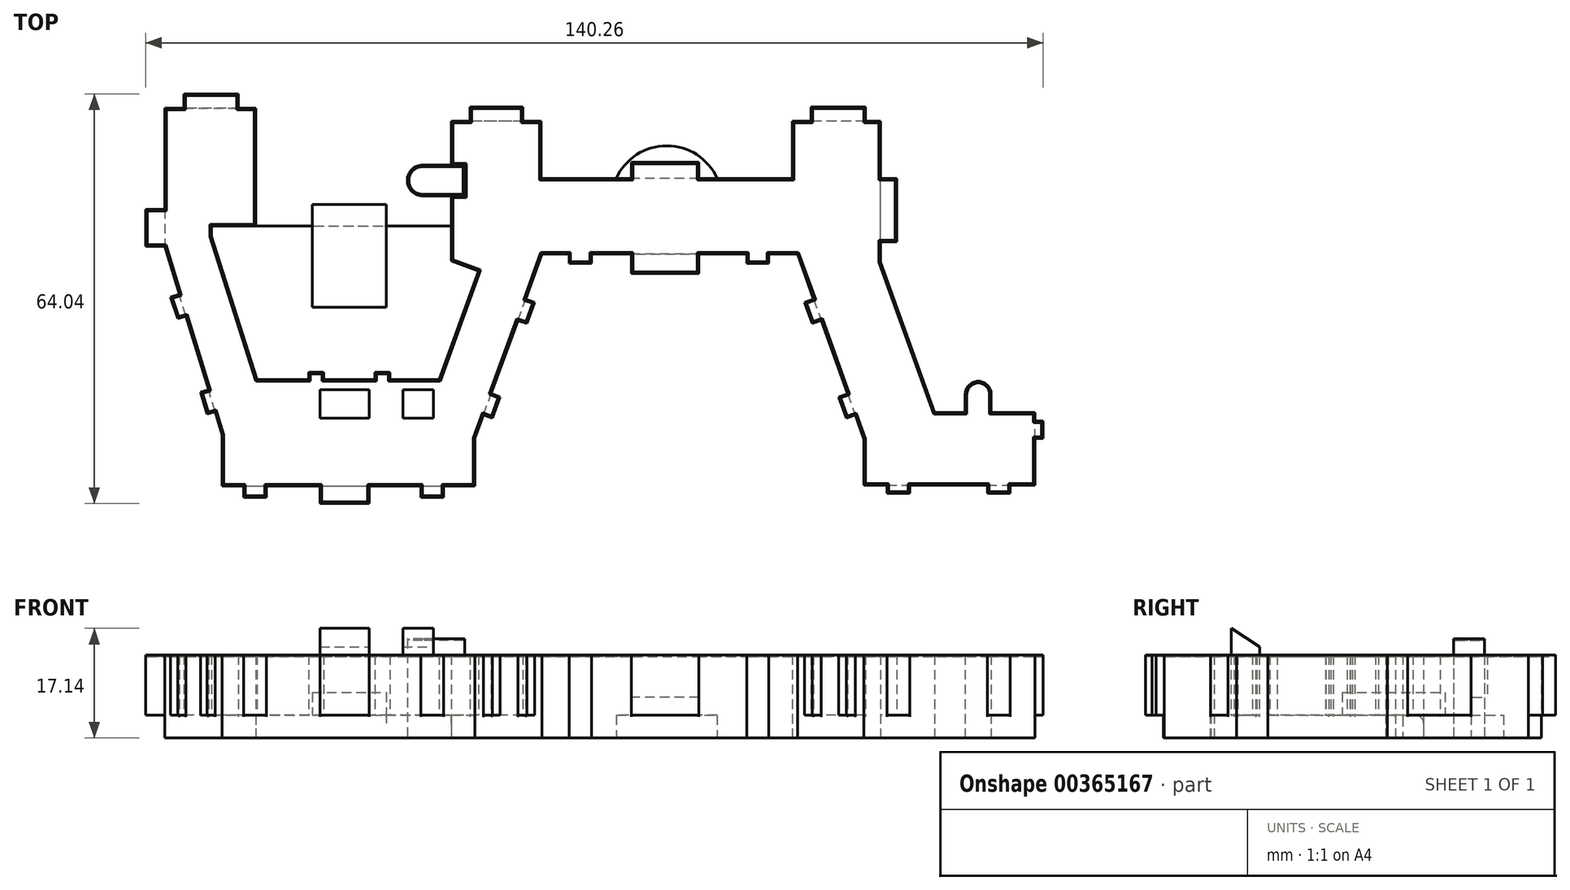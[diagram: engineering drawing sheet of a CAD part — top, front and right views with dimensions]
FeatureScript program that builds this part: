
annotation { "Feature Type Name" : "Feature", "Feature Type Description" : "" }
export const myFeature = defineFeature(function(context is Context, id is Id, definition is map)
    precondition{}
    {
        {
            var Q0;
            Q0=qCreatedBy(makeId("Top.planeOp"),FACE);
            var sketch = newSketch(context, id + "F0", { "sketchPlane" : qUnion([Q0])});
            skLineSegment(sketch, "E0", {"start": v(11.22, -2.24) * mm, "end": v(8.5, -2.24) * mm});
            skLineSegment(sketch, "E1", {"start": v(8.5, -2.24) * mm, "end": v(8.5, 0) * mm});
            skLineSegment(sketch, "E2", {"start": v(8.5, 0) * mm, "end": v(0, 0) * mm});
            skLineSegment(sketch, "E3", {"start": v(0, 0) * mm, "end": v(0, -2.24) * mm});
            skLineSegment(sketch, "E4", {"start": v(0, -2.24) * mm, "end": v(-3.01, -2.24) * mm});
            skLineSegment(sketch, "E5", {"start": v(-3.01, -2.24) * mm, "end": v(-3.01, -18.02) * mm});
            skLineSegment(sketch, "E6", {"start": v(-3.01, -18.02) * mm, "end": v(-6, -18.02) * mm});
            skLineSegment(sketch, "E7", {"start": v(-6, -18.02) * mm, "end": v(-6, -23.84) * mm});
            skLineSegment(sketch, "E8", {"start": v(-6, -23.84) * mm, "end": v(-3.01, -23.84) * mm});
            skLineSegment(sketch, "E9", {"start": v(-3.01, -23.84) * mm, "end": v(-0.72, -31.34) * mm});
            skLineSegment(sketch, "E10", {"start": v(-0.72, -31.34) * mm, "end": v(-2.13, -31.77) * mm});
            skLineSegment(sketch, "E11", {"start": v(-2.13, -31.77) * mm, "end": v(-0.97, -35.12) * mm});
            skLineSegment(sketch, "E12", {"start": v(-0.97, -35.12) * mm, "end": v(0.32, -34.73) * mm});
            skLineSegment(sketch, "E13", {"start": v(0.32, -34.73) * mm, "end": v(3.84, -46.26) * mm});
            skLineSegment(sketch, "E14", {"start": v(3.84, -46.26) * mm, "end": v(2.58, -46.65) * mm});
            skLineSegment(sketch, "E15", {"start": v(2.58, -46.65) * mm, "end": v(3.62, -50.04) * mm});
            skLineSegment(sketch, "E16", {"start": v(3.62, -50.04) * mm, "end": v(4.88, -49.65) * mm});
            skLineSegment(sketch, "E17", {"start": v(4.88, -49.65) * mm, "end": v(6, -53.3) * mm});
            skLineSegment(sketch, "E18", {"start": v(6, -53.3) * mm, "end": v(6, -61.28) * mm});
            skLineSegment(sketch, "E19", {"start": v(6, -61.28) * mm, "end": v(9.31, -61.28) * mm});
            skLineSegment(sketch, "E20", {"start": v(9.31, -61.28) * mm, "end": v(9.31, -63.05) * mm});
            skLineSegment(sketch, "E21", {"start": v(9.31, -63.05) * mm, "end": v(12.86, -63.05) * mm});
            skLineSegment(sketch, "E22", {"start": v(12.86, -63.05) * mm, "end": v(12.86, -61.28) * mm});
            skLineSegment(sketch, "E23", {"start": v(12.86, -61.28) * mm, "end": v(21.27, -61.28) * mm});
            skLineSegment(sketch, "E24", {"start": v(21.27, -61.28) * mm, "end": v(21.27, -64.04) * mm});
            skLineSegment(sketch, "E25", {"start": v(21.27, -64.04) * mm, "end": v(28.97, -64.04) * mm});
            skLineSegment(sketch, "E26", {"start": v(28.97, -64.04) * mm, "end": v(28.97, -61.28) * mm});
            skLineSegment(sketch, "E27", {"start": v(28.97, -61.28) * mm, "end": v(37, -61.28) * mm});
            skLineSegment(sketch, "E28", {"start": v(37, -61.28) * mm, "end": v(37, -63.05) * mm});
            skLineSegment(sketch, "E29", {"start": v(37, -63.05) * mm, "end": v(40.54, -63.05) * mm});
            skLineSegment(sketch, "E30", {"start": v(40.54, -63.05) * mm, "end": v(40.54, -61.28) * mm});
            skLineSegment(sketch, "E31", {"start": v(40.54, -61.28) * mm, "end": v(45.48, -61.28) * mm});
            skLineSegment(sketch, "E32", {"start": v(45.48, -61.28) * mm, "end": v(45.48, -53.82) * mm});
            skLineSegment(sketch, "E33", {"start": v(45.48, -53.82) * mm, "end": v(46.82, -50.15) * mm});
            skLineSegment(sketch, "E34", {"start": v(46.82, -50.15) * mm, "end": v(48.2, -50.7) * mm});
            skLineSegment(sketch, "E35", {"start": v(48.2, -50.7) * mm, "end": v(49.42, -47.37) * mm});
            skLineSegment(sketch, "E36", {"start": v(49.42, -47.37) * mm, "end": v(48.03, -46.82) * mm});
            skLineSegment(sketch, "E37", {"start": v(48.03, -46.82) * mm, "end": v(52.17, -35.43) * mm});
            skLineSegment(sketch, "E38", {"start": v(52.17, -35.43) * mm, "end": v(53.6, -35.9) * mm});
            skLineSegment(sketch, "E39", {"start": v(53.6, -35.9) * mm, "end": v(54.8, -32.57) * mm});
            skLineSegment(sketch, "E40", {"start": v(54.8, -32.57) * mm, "end": v(53.38, -32.1) * mm});
            skLineSegment(sketch, "E41", {"start": v(53.38, -32.1) * mm, "end": v(55.96, -25.02) * mm});
            skLineSegment(sketch, "E42", {"start": v(55.96, -25.02) * mm, "end": v(60.16, -25.02) * mm});
            skLineSegment(sketch, "E43", {"start": v(60.16, -25.02) * mm, "end": v(60.16, -26.52) * mm});
            skLineSegment(sketch, "E44", {"start": v(60.16, -26.52) * mm, "end": v(63.7, -26.52) * mm});
            skLineSegment(sketch, "E45", {"start": v(63.7, -26.52) * mm, "end": v(63.7, -25.02) * mm});
            skLineSegment(sketch, "E46", {"start": v(63.7, -25.02) * mm, "end": v(69.91, -25.02) * mm});
            skLineSegment(sketch, "E47", {"start": v(69.91, -25.02) * mm, "end": v(69.91, -28.1) * mm});
            skLineSegment(sketch, "E48", {"start": v(69.91, -28.1) * mm, "end": v(80.46, -28.1) * mm});
            skLineSegment(sketch, "E49", {"start": v(80.46, -28.1) * mm, "end": v(80.46, -25.02) * mm});
            skLineSegment(sketch, "E50", {"start": v(80.46, -25.02) * mm, "end": v(87.96, -25.02) * mm});
            skLineSegment(sketch, "E51", {"start": v(87.96, -25.02) * mm, "end": v(87.96, -26.52) * mm});
            skLineSegment(sketch, "E52", {"start": v(87.96, -26.52) * mm, "end": v(91.4, -26.52) * mm});
            skLineSegment(sketch, "E53", {"start": v(91.4, -26.52) * mm, "end": v(91.4, -25.02) * mm});
            skLineSegment(sketch, "E54", {"start": v(91.4, -25.02) * mm, "end": v(95.85, -25.02) * mm});
            skLineSegment(sketch, "E55", {"start": v(95.85, -25.02) * mm, "end": v(98.38, -32.06) * mm});
            skLineSegment(sketch, "E56", {"start": v(98.38, -32.06) * mm, "end": v(96.97, -32.57) * mm});
            skLineSegment(sketch, "E57", {"start": v(96.97, -32.57) * mm, "end": v(98.17, -35.9) * mm});
            skLineSegment(sketch, "E58", {"start": v(98.17, -35.9) * mm, "end": v(99.58, -35.4) * mm});
            skLineSegment(sketch, "E59", {"start": v(99.58, -35.4) * mm, "end": v(103.7, -46.87) * mm});
            skLineSegment(sketch, "E60", {"start": v(103.7, -46.87) * mm, "end": v(102.29, -47.37) * mm});
            skLineSegment(sketch, "E61", {"start": v(102.29, -47.37) * mm, "end": v(103.49, -50.7) * mm});
            skLineSegment(sketch, "E62", {"start": v(103.49, -50.7) * mm, "end": v(104.9, -50.2) * mm});
            skLineSegment(sketch, "E63", {"start": v(104.9, -50.2) * mm, "end": v(106.25, -53.96) * mm});
            skLineSegment(sketch, "E64", {"start": v(106.25, -53.96) * mm, "end": v(106.25, -61.16) * mm});
            skLineSegment(sketch, "E65", {"start": v(106.25, -61.16) * mm, "end": v(109.85, -61.16) * mm});
            skLineSegment(sketch, "E66", {"start": v(109.85, -61.16) * mm, "end": v(109.85, -62.43) * mm});
            skLineSegment(sketch, "E67", {"start": v(109.85, -62.43) * mm, "end": v(113.4, -62.43) * mm});
            skLineSegment(sketch, "E68", {"start": v(113.4, -62.43) * mm, "end": v(113.4, -61.16) * mm});
            skLineSegment(sketch, "E69", {"start": v(113.4, -61.16) * mm, "end": v(125.52, -61.16) * mm});
            skLineSegment(sketch, "E70", {"start": v(125.52, -61.16) * mm, "end": v(125.52, -62.43) * mm});
            skLineSegment(sketch, "E71", {"start": v(125.52, -62.43) * mm, "end": v(129.06, -62.43) * mm});
            skLineSegment(sketch, "E72", {"start": v(129.06, -62.43) * mm, "end": v(129.06, -61.16) * mm});
            skLineSegment(sketch, "E73", {"start": v(129.06, -61.16) * mm, "end": v(133, -61.16) * mm});
            skLineSegment(sketch, "E74", {"start": v(133, -61.16) * mm, "end": v(133, -53.89) * mm});
            skLineSegment(sketch, "E75", {"start": v(133, -53.89) * mm, "end": v(134.26, -53.89) * mm});
            skLineSegment(sketch, "E76", {"start": v(134.26, -53.89) * mm, "end": v(134.26, -51.15) * mm});
            skLineSegment(sketch, "E77", {"start": v(134.26, -51.15) * mm, "end": v(133, -51.15) * mm});
            skLineSegment(sketch, "E78", {"start": v(133, -51.15) * mm, "end": v(133, -49.82) * mm});
            skLineSegment(sketch, "E79", {"start": v(133, -49.82) * mm, "end": v(126.13, -49.82) * mm});
            skLineSegment(sketch, "E80", {"start": v(126.13, -49.82) * mm, "end": v(126.13, -46.96) * mm});
            skLineSegment(sketch, "E81", {"start": v(122.07, -46.96) * mm, "end": v(122.07, -49.82) * mm});
            skLineSegment(sketch, "E82", {"start": v(122.07, -49.82) * mm, "end": v(117.3, -49.82) * mm});
            skLineSegment(sketch, "E83", {"start": v(117.3, -49.82) * mm, "end": v(108.85, -26.28) * mm});
            skLineSegment(sketch, "E84", {"start": v(108.85, -26.28) * mm, "end": v(108.85, -23.13) * mm});
            skLineSegment(sketch, "E85", {"start": v(108.85, -23.13) * mm, "end": v(111.35, -23.13) * mm});
            skLineSegment(sketch, "E86", {"start": v(111.35, -23.13) * mm, "end": v(111.35, -13.22) * mm});
            skLineSegment(sketch, "E87", {"start": v(111.35, -13.22) * mm, "end": v(108.85, -13.22) * mm});
            skLineSegment(sketch, "E88", {"start": v(108.85, -13.22) * mm, "end": v(108.85, -4.25) * mm});
            skLineSegment(sketch, "E89", {"start": v(108.85, -4.25) * mm, "end": v(106.47, -4.25) * mm});
            skLineSegment(sketch, "E90", {"start": v(106.47, -4.25) * mm, "end": v(106.47, -2.03) * mm});
            skLineSegment(sketch, "E91", {"start": v(106.47, -2.03) * mm, "end": v(98, -2.03) * mm});
            skLineSegment(sketch, "E92", {"start": v(98, -2.03) * mm, "end": v(98, -4.25) * mm});
            skLineSegment(sketch, "E93", {"start": v(98, -4.25) * mm, "end": v(95.07, -4.25) * mm});
            skLineSegment(sketch, "E94", {"start": v(95.07, -4.25) * mm, "end": v(95.07, -13.22) * mm});
            skLineSegment(sketch, "E95", {"start": v(95.07, -13.22) * mm, "end": v(80.46, -13.22) * mm});
            skLineSegment(sketch, "E96", {"start": v(80.46, -13.22) * mm, "end": v(80.46, -10.66) * mm});
            skLineSegment(sketch, "E97", {"start": v(80.46, -10.66) * mm, "end": v(69.91, -10.66) * mm});
            skLineSegment(sketch, "E98", {"start": v(69.91, -10.66) * mm, "end": v(69.91, -13.22) * mm});
            skLineSegment(sketch, "E99", {"start": v(69.91, -13.22) * mm, "end": v(55.8, -13.22) * mm});
            skLineSegment(sketch, "E100", {"start": v(55.8, -13.22) * mm, "end": v(55.8, -4.25) * mm});
            skLineSegment(sketch, "E101", {"start": v(55.8, -4.25) * mm, "end": v(52.93, -4.25) * mm});
            skLineSegment(sketch, "E102", {"start": v(52.93, -4.25) * mm, "end": v(52.93, -2.03) * mm});
            skLineSegment(sketch, "E103", {"start": v(52.93, -2.03) * mm, "end": v(44.68, -2.03) * mm});
            skLineSegment(sketch, "E104", {"start": v(44.68, -2.03) * mm, "end": v(44.68, -4.25) * mm});
            skLineSegment(sketch, "E105", {"start": v(44.68, -4.25) * mm, "end": v(41.8, -4.25) * mm});
            skLineSegment(sketch, "E106", {"start": v(41.8, -4.25) * mm, "end": v(41.8, -11.12) * mm});
            skLineSegment(sketch, "E107", {"start": v(41.8, -11.12) * mm, "end": v(37.3, -11.12) * mm});
            skLineSegment(sketch, "E108", {"start": v(37.3, -15.94) * mm, "end": v(41.79, -15.94) * mm});
            skLineSegment(sketch, "E109", {"start": v(41.79, -15.94) * mm, "end": v(41.79, -26.13) * mm});
            skLineSegment(sketch, "E110", {"start": v(41.79, -26.13) * mm, "end": v(46.05, -27.68) * mm});
            skLineSegment(sketch, "E111", {"start": v(46.05, -27.68) * mm, "end": v(39.88, -44.65) * mm});
            skLineSegment(sketch, "E112", {"start": v(39.88, -44.65) * mm, "end": v(32.18, -44.65) * mm});
            skLineSegment(sketch, "E113", {"start": v(32.18, -44.65) * mm, "end": v(32.18, -43.48) * mm});
            skLineSegment(sketch, "E114", {"start": v(32.18, -43.48) * mm, "end": v(29.86, -43.48) * mm});
            skLineSegment(sketch, "E115", {"start": v(29.86, -43.48) * mm, "end": v(29.86, -44.65) * mm});
            skLineSegment(sketch, "E116", {"start": v(29.86, -44.65) * mm, "end": v(21.83, -44.65) * mm});
            skLineSegment(sketch, "E117", {"start": v(21.83, -44.65) * mm, "end": v(21.83, -43.48) * mm});
            skLineSegment(sketch, "E118", {"start": v(21.83, -43.48) * mm, "end": v(19.5, -43.48) * mm});
            skLineSegment(sketch, "E119", {"start": v(19.5, -43.48) * mm, "end": v(19.5, -44.65) * mm});
            skLineSegment(sketch, "E120", {"start": v(19.5, -44.65) * mm, "end": v(11.42, -44.65) * mm});
            skLineSegment(sketch, "E121", {"start": v(11.42, -44.65) * mm, "end": v(4.3, -22.29) * mm});
            skLineSegment(sketch, "E122", {"start": v(4.3, -22.29) * mm, "end": v(4.3, -20.63) * mm});
            skLineSegment(sketch, "E123", {"start": v(4.3, -20.63) * mm, "end": v(11.22, -20.63) * mm});
            skLineSegment(sketch, "E124", {"start": v(11.22, -20.63) * mm, "end": v(11.22, -2.24) * mm});
            skArc(sketch, "E125", {"start": v(37.3, -11.12) * mm, "mid": v(34.9, -13.53) * mm, "end": v(37.3, -15.94) * mm});
            skArc(sketch, "E126", {"start": v(126.13, -46.96) * mm, "mid": v(124.1, -44.93) * mm, "end": v(122.07, -46.96) * mm});
            skLineSegment(sketch, "E127", {"start": v(41.8, -11.12) * mm, "end": v(43.9, -11.12) * mm});
            skLineSegment(sketch, "E128", {"start": v(43.9, -11.12) * mm, "end": v(43.9, -15.94) * mm});
            skLineSegment(sketch, "E129", {"start": v(43.9, -15.94) * mm, "end": v(41.79, -15.94) * mm});
            skLineSegment(sketch, "E130", {"start": v(-3.01, -18.02) * mm, "end": v(-3.01, -23.84) * mm, "construction": true});
            skSolve(sketch);
        }
        {
            var Q0;
            Q0=qSketchRegion(id+"F0",true);
            extrude(context, id + "F1", {"entities" : qUnion([Q0]), "depth" : 12.7 * mm});
        }
        {
            var Q0;
            Q0=makeQuery(id+"F0.imprint","IMPRINT",FACE,{"disambiguationData":[TD([[makeQuery(id+"F0.imprint","IMPRINT",EDGE,{"derivedFrom":sQuery(id+"F0.wireOp",EDGE,"E107")}),1.0]])]});
            extrude(context, id + "F2", {"entities" : qUnion([Q0]), "operationType" : NewBodyOperationType.ADD, "depth" : 15.24 * mm});
        }
        {
            var Q0;
            Q0=makeQuery(id+"F1.opExtrude","CAP_FACE",FACE,{"disambiguationData":[OSD([sQuery(id+"F0.wireOp",EDGE,"E0"),sQuery(id+"F0.wireOp",EDGE,"E1"),sQuery(id+"F0.wireOp",EDGE,"E2"),sQuery(id+"F0.wireOp",EDGE,"E3"),sQuery(id+"F0.wireOp",EDGE,"E4"),sQuery(id+"F0.wireOp",EDGE,"E5"),sQuery(id+"F0.wireOp",EDGE,"E6"),sQuery(id+"F0.wireOp",EDGE,"E7"),sQuery(id+"F0.wireOp",EDGE,"E8"),sQuery(id+"F0.wireOp",EDGE,"E9"),sQuery(id+"F0.wireOp",EDGE,"E10"),sQuery(id+"F0.wireOp",EDGE,"E11"),sQuery(id+"F0.wireOp",EDGE,"E12"),sQuery(id+"F0.wireOp",EDGE,"E13"),sQuery(id+"F0.wireOp",EDGE,"E14"),sQuery(id+"F0.wireOp",EDGE,"E15"),sQuery(id+"F0.wireOp",EDGE,"E16"),sQuery(id+"F0.wireOp",EDGE,"E17"),sQuery(id+"F0.wireOp",EDGE,"E18"),sQuery(id+"F0.wireOp",EDGE,"E19"),sQuery(id+"F0.wireOp",EDGE,"E20"),sQuery(id+"F0.wireOp",EDGE,"E21"),sQuery(id+"F0.wireOp",EDGE,"E22"),sQuery(id+"F0.wireOp",EDGE,"E23"),sQuery(id+"F0.wireOp",EDGE,"E24"),sQuery(id+"F0.wireOp",EDGE,"E25"),sQuery(id+"F0.wireOp",EDGE,"E26"),sQuery(id+"F0.wireOp",EDGE,"E27"),sQuery(id+"F0.wireOp",EDGE,"E28"),sQuery(id+"F0.wireOp",EDGE,"E29"),sQuery(id+"F0.wireOp",EDGE,"E30"),sQuery(id+"F0.wireOp",EDGE,"E31"),sQuery(id+"F0.wireOp",EDGE,"E32"),sQuery(id+"F0.wireOp",EDGE,"E33"),sQuery(id+"F0.wireOp",EDGE,"E34"),sQuery(id+"F0.wireOp",EDGE,"E35"),sQuery(id+"F0.wireOp",EDGE,"E36"),sQuery(id+"F0.wireOp",EDGE,"E37"),sQuery(id+"F0.wireOp",EDGE,"E38"),sQuery(id+"F0.wireOp",EDGE,"E39"),sQuery(id+"F0.wireOp",EDGE,"E40"),sQuery(id+"F0.wireOp",EDGE,"E41"),sQuery(id+"F0.wireOp",EDGE,"E42"),sQuery(id+"F0.wireOp",EDGE,"E43"),sQuery(id+"F0.wireOp",EDGE,"E44"),sQuery(id+"F0.wireOp",EDGE,"E45"),sQuery(id+"F0.wireOp",EDGE,"E46"),sQuery(id+"F0.wireOp",EDGE,"E47"),sQuery(id+"F0.wireOp",EDGE,"E48"),sQuery(id+"F0.wireOp",EDGE,"E49"),sQuery(id+"F0.wireOp",EDGE,"E50"),sQuery(id+"F0.wireOp",EDGE,"E51"),sQuery(id+"F0.wireOp",EDGE,"E52"),sQuery(id+"F0.wireOp",EDGE,"E53"),sQuery(id+"F0.wireOp",EDGE,"E54"),sQuery(id+"F0.wireOp",EDGE,"E55"),sQuery(id+"F0.wireOp",EDGE,"E56"),sQuery(id+"F0.wireOp",EDGE,"E57"),sQuery(id+"F0.wireOp",EDGE,"E58"),sQuery(id+"F0.wireOp",EDGE,"E59"),sQuery(id+"F0.wireOp",EDGE,"E60"),sQuery(id+"F0.wireOp",EDGE,"E61"),sQuery(id+"F0.wireOp",EDGE,"E62"),sQuery(id+"F0.wireOp",EDGE,"E63"),sQuery(id+"F0.wireOp",EDGE,"E64"),sQuery(id+"F0.wireOp",EDGE,"E65"),sQuery(id+"F0.wireOp",EDGE,"E66"),sQuery(id+"F0.wireOp",EDGE,"E67"),sQuery(id+"F0.wireOp",EDGE,"E68"),sQuery(id+"F0.wireOp",EDGE,"E69"),sQuery(id+"F0.wireOp",EDGE,"E70"),sQuery(id+"F0.wireOp",EDGE,"E71"),sQuery(id+"F0.wireOp",EDGE,"E72"),sQuery(id+"F0.wireOp",EDGE,"E73"),sQuery(id+"F0.wireOp",EDGE,"E74"),sQuery(id+"F0.wireOp",EDGE,"E75"),sQuery(id+"F0.wireOp",EDGE,"E76"),sQuery(id+"F0.wireOp",EDGE,"E77"),sQuery(id+"F0.wireOp",EDGE,"E78"),sQuery(id+"F0.wireOp",EDGE,"E79"),sQuery(id+"F0.wireOp",EDGE,"E80"),sQuery(id+"F0.wireOp",EDGE,"E81"),sQuery(id+"F0.wireOp",EDGE,"E82"),sQuery(id+"F0.wireOp",EDGE,"E83"),sQuery(id+"F0.wireOp",EDGE,"E84"),sQuery(id+"F0.wireOp",EDGE,"E85"),sQuery(id+"F0.wireOp",EDGE,"E86"),sQuery(id+"F0.wireOp",EDGE,"E87"),sQuery(id+"F0.wireOp",EDGE,"E88"),sQuery(id+"F0.wireOp",EDGE,"E89"),sQuery(id+"F0.wireOp",EDGE,"E90"),sQuery(id+"F0.wireOp",EDGE,"E91"),sQuery(id+"F0.wireOp",EDGE,"E92"),sQuery(id+"F0.wireOp",EDGE,"E93"),sQuery(id+"F0.wireOp",EDGE,"E94"),sQuery(id+"F0.wireOp",EDGE,"E95"),sQuery(id+"F0.wireOp",EDGE,"E96"),sQuery(id+"F0.wireOp",EDGE,"E97"),sQuery(id+"F0.wireOp",EDGE,"E98"),sQuery(id+"F0.wireOp",EDGE,"E99"),sQuery(id+"F0.wireOp",EDGE,"E100"),sQuery(id+"F0.wireOp",EDGE,"E101"),sQuery(id+"F0.wireOp",EDGE,"E102"),sQuery(id+"F0.wireOp",EDGE,"E103"),sQuery(id+"F0.wireOp",EDGE,"E104"),sQuery(id+"F0.wireOp",EDGE,"E105"),sQuery(id+"F0.wireOp",EDGE,"E106"),sQuery(id+"F0.wireOp",EDGE,"E107"),sQuery(id+"F0.wireOp",EDGE,"E108"),sQuery(id+"F0.wireOp",EDGE,"E109"),sQuery(id+"F0.wireOp",EDGE,"E110"),sQuery(id+"F0.wireOp",EDGE,"E111"),sQuery(id+"F0.wireOp",EDGE,"E112"),sQuery(id+"F0.wireOp",EDGE,"E113"),sQuery(id+"F0.wireOp",EDGE,"E114"),sQuery(id+"F0.wireOp",EDGE,"E115"),sQuery(id+"F0.wireOp",EDGE,"E116"),sQuery(id+"F0.wireOp",EDGE,"E117"),sQuery(id+"F0.wireOp",EDGE,"E118"),sQuery(id+"F0.wireOp",EDGE,"E119"),sQuery(id+"F0.wireOp",EDGE,"E120"),sQuery(id+"F0.wireOp",EDGE,"E121"),sQuery(id+"F0.wireOp",EDGE,"E122"),sQuery(id+"F0.wireOp",EDGE,"E123"),sQuery(id+"F0.wireOp",EDGE,"E124"),sQuery(id+"F0.wireOp",EDGE,"E125"),sQuery(id+"F0.wireOp",EDGE,"E126")])],"isStart":false});
            var sketch = newSketch(context, id + "F3", { "sketchPlane" : qUnion([Q0])});
            skLineSegment(sketch, "E131.0", {"start": v(42.05, -4.5) * mm, "end": v(42.05, -10.87) * mm});
            skLineSegment(sketch, "E131.1", {"start": v(44.93, -4.5) * mm, "end": v(42.05, -4.5) * mm});
            skLineSegment(sketch, "E131.2", {"start": v(44.93, -2.28) * mm, "end": v(44.93, -4.5) * mm});
            skLineSegment(sketch, "E131.3", {"start": v(52.68, -2.28) * mm, "end": v(44.93, -2.28) * mm});
            skLineSegment(sketch, "E131.4", {"start": v(52.68, -4.5) * mm, "end": v(52.68, -2.28) * mm});
            skLineSegment(sketch, "E131.5", {"start": v(55.56, -4.5) * mm, "end": v(52.68, -4.5) * mm});
            skLineSegment(sketch, "E131.6", {"start": v(55.56, -13.47) * mm, "end": v(55.56, -4.5) * mm});
            skLineSegment(sketch, "E131.7", {"start": v(70.17, -13.47) * mm, "end": v(55.56, -13.47) * mm});
            skLineSegment(sketch, "E131.8", {"start": v(70.17, -10.91) * mm, "end": v(70.17, -13.47) * mm});
            skLineSegment(sketch, "E131.9", {"start": v(80.2, -10.91) * mm, "end": v(70.17, -10.91) * mm});
            skLineSegment(sketch, "E131.10", {"start": v(80.2, -13.47) * mm, "end": v(80.2, -10.91) * mm});
            skLineSegment(sketch, "E131.11", {"start": v(95.32, -13.47) * mm, "end": v(80.2, -13.47) * mm});
            skLineSegment(sketch, "E131.12", {"start": v(95.32, -4.5) * mm, "end": v(95.32, -13.47) * mm});
            skLineSegment(sketch, "E131.13", {"start": v(98.26, -4.5) * mm, "end": v(95.32, -4.5) * mm});
            skLineSegment(sketch, "E131.14", {"start": v(98.26, -2.28) * mm, "end": v(98.26, -4.5) * mm});
            skLineSegment(sketch, "E131.15", {"start": v(106.22, -2.28) * mm, "end": v(98.26, -2.28) * mm});
            skLineSegment(sketch, "E131.16", {"start": v(106.22, -4.5) * mm, "end": v(106.22, -2.28) * mm});
            skLineSegment(sketch, "E131.17", {"start": v(108.6, -4.5) * mm, "end": v(106.22, -4.5) * mm});
            skLineSegment(sketch, "E131.18", {"start": v(108.6, -13.47) * mm, "end": v(108.6, -4.5) * mm});
            skLineSegment(sketch, "E131.19", {"start": v(111.1, -13.47) * mm, "end": v(108.6, -13.47) * mm});
            skLineSegment(sketch, "E131.20", {"start": v(111.1, -22.87) * mm, "end": v(111.1, -13.47) * mm});
            skLineSegment(sketch, "E131.21", {"start": v(108.6, -22.87) * mm, "end": v(111.1, -22.87) * mm});
            skLineSegment(sketch, "E131.22", {"start": v(108.6, -26.33) * mm, "end": v(108.6, -22.87) * mm});
            skLineSegment(sketch, "E131.23", {"start": v(117.13, -50.07) * mm, "end": v(108.6, -26.33) * mm});
            skLineSegment(sketch, "E131.24", {"start": v(122.32, -50.07) * mm, "end": v(117.13, -50.07) * mm});
            skLineSegment(sketch, "E131.25", {"start": v(122.32, -46.96) * mm, "end": v(122.32, -50.07) * mm});
            skArc(sketch, "E131.26", {"start": v(125.87, -46.96) * mm, "mid": v(124.1, -45.19) * mm, "end": v(122.32, -46.96) * mm});
            skLineSegment(sketch, "E131.27", {"start": v(125.87, -50.07) * mm, "end": v(125.87, -46.96) * mm});
            skLineSegment(sketch, "E131.28", {"start": v(132.74, -50.07) * mm, "end": v(125.87, -50.07) * mm});
            skLineSegment(sketch, "E131.29", {"start": v(132.74, -51.4) * mm, "end": v(132.74, -50.07) * mm});
            skLineSegment(sketch, "E131.30", {"start": v(28.72, -61.02) * mm, "end": v(37.25, -61.02) * mm});
            skLineSegment(sketch, "E131.31", {"start": v(28.72, -63.8) * mm, "end": v(28.72, -61.02) * mm});
            skLineSegment(sketch, "E131.32", {"start": v(21.53, -63.8) * mm, "end": v(28.72, -63.8) * mm});
            skLineSegment(sketch, "E131.33", {"start": v(21.53, -61.02) * mm, "end": v(21.53, -63.8) * mm});
            skLineSegment(sketch, "E131.34", {"start": v(12.6, -61.02) * mm, "end": v(21.53, -61.02) * mm});
            skLineSegment(sketch, "E131.35", {"start": v(12.6, -62.8) * mm, "end": v(12.6, -61.02) * mm});
            skLineSegment(sketch, "E131.36", {"start": v(9.57, -62.8) * mm, "end": v(12.6, -62.8) * mm});
            skLineSegment(sketch, "E131.37", {"start": v(9.57, -61.02) * mm, "end": v(9.57, -62.8) * mm});
            skLineSegment(sketch, "E131.38", {"start": v(6.25, -61.02) * mm, "end": v(9.57, -61.02) * mm});
            skLineSegment(sketch, "E131.39", {"start": v(6.25, -53.27) * mm, "end": v(6.25, -61.02) * mm});
            skLineSegment(sketch, "E131.40", {"start": v(5.04, -49.34) * mm, "end": v(6.25, -53.27) * mm});
            skLineSegment(sketch, "E131.41", {"start": v(3.79, -49.72) * mm, "end": v(5.04, -49.34) * mm});
            skLineSegment(sketch, "E131.42", {"start": v(2.9, -46.82) * mm, "end": v(3.79, -49.72) * mm});
            skLineSegment(sketch, "E131.43", {"start": v(4.16, -46.43) * mm, "end": v(2.9, -46.82) * mm});
            skLineSegment(sketch, "E131.44", {"start": v(0.48, -34.4) * mm, "end": v(4.16, -46.43) * mm});
            skLineSegment(sketch, "E131.45", {"start": v(-0.81, -34.8) * mm, "end": v(0.48, -34.4) * mm});
            skLineSegment(sketch, "E131.46", {"start": v(-1.8, -31.94) * mm, "end": v(-0.81, -34.8) * mm});
            skLineSegment(sketch, "E131.47", {"start": v(-0.4, -31.5) * mm, "end": v(-1.8, -31.94) * mm});
            skLineSegment(sketch, "E131.48", {"start": v(-2.82, -23.58) * mm, "end": v(-0.4, -31.5) * mm});
            skLineSegment(sketch, "E131.49", {"start": v(-5.75, -23.58) * mm, "end": v(-2.82, -23.58) * mm});
            skLineSegment(sketch, "E131.50", {"start": v(-5.75, -18.28) * mm, "end": v(-5.75, -23.58) * mm});
            skLineSegment(sketch, "E131.51", {"start": v(-2.76, -18.28) * mm, "end": v(-5.75, -18.28) * mm});
            skLineSegment(sketch, "E131.52", {"start": v(-2.76, -2.5) * mm, "end": v(-2.76, -18.28) * mm});
            skLineSegment(sketch, "E131.53", {"start": v(0.25, -2.5) * mm, "end": v(-2.76, -2.5) * mm});
            skLineSegment(sketch, "E131.54", {"start": v(30.1, -44.9) * mm, "end": v(21.57, -44.9) * mm});
            skLineSegment(sketch, "E131.55", {"start": v(30.1, -43.74) * mm, "end": v(30.1, -44.9) * mm});
            skLineSegment(sketch, "E131.56", {"start": v(31.93, -43.74) * mm, "end": v(30.1, -43.74) * mm});
            skLineSegment(sketch, "E131.57", {"start": v(31.93, -44.9) * mm, "end": v(31.93, -43.74) * mm});
            skLineSegment(sketch, "E131.58", {"start": v(40.06, -44.9) * mm, "end": v(31.93, -44.9) * mm});
            skLineSegment(sketch, "E131.59", {"start": v(46.37, -27.52) * mm, "end": v(40.06, -44.9) * mm});
            skLineSegment(sketch, "E131.60", {"start": v(44.16, -10.87) * mm, "end": v(44.16, -16.2) * mm});
            skLineSegment(sketch, "E131.61", {"start": v(44.16, -16.2) * mm, "end": v(42.04, -16.2) * mm});
            skLineSegment(sketch, "E131.62", {"start": v(42.04, -16.2) * mm, "end": v(42.04, -25.95) * mm});
            skLineSegment(sketch, "E131.63", {"start": v(42.04, -25.95) * mm, "end": v(46.37, -27.52) * mm});
            skLineSegment(sketch, "E131.64", {"start": v(21.57, -44.9) * mm, "end": v(21.57, -43.74) * mm});
            skLineSegment(sketch, "E131.65", {"start": v(21.57, -43.74) * mm, "end": v(19.76, -43.74) * mm});
            skLineSegment(sketch, "E131.66", {"start": v(19.76, -43.74) * mm, "end": v(19.76, -44.9) * mm});
            skLineSegment(sketch, "E131.67", {"start": v(19.76, -44.9) * mm, "end": v(11.23, -44.9) * mm});
            skLineSegment(sketch, "E131.68", {"start": v(11.23, -44.9) * mm, "end": v(4.04, -22.33) * mm});
            skLineSegment(sketch, "E131.69", {"start": v(4.04, -22.33) * mm, "end": v(4.04, -20.37) * mm});
            skLineSegment(sketch, "E131.70", {"start": v(4.04, -20.37) * mm, "end": v(10.96, -20.37) * mm});
            skLineSegment(sketch, "E131.71", {"start": v(10.96, -20.37) * mm, "end": v(10.96, -2.5) * mm});
            skLineSegment(sketch, "E131.72", {"start": v(10.96, -2.5) * mm, "end": v(8.25, -2.5) * mm});
            skLineSegment(sketch, "E131.73", {"start": v(8.25, -2.5) * mm, "end": v(8.25, -0.25) * mm});
            skLineSegment(sketch, "E131.74", {"start": v(8.25, -0.25) * mm, "end": v(0.25, -0.25) * mm});
            skLineSegment(sketch, "E131.75", {"start": v(0.25, -0.25) * mm, "end": v(0.25, -2.5) * mm});
            skLineSegment(sketch, "E131.76", {"start": v(37.25, -61.02) * mm, "end": v(37.25, -62.8) * mm});
            skLineSegment(sketch, "E131.77", {"start": v(37.25, -62.8) * mm, "end": v(40.29, -62.8) * mm});
            skLineSegment(sketch, "E131.78", {"start": v(40.29, -62.8) * mm, "end": v(40.29, -61.02) * mm});
            skLineSegment(sketch, "E131.79", {"start": v(40.29, -61.02) * mm, "end": v(45.23, -61.02) * mm});
            skLineSegment(sketch, "E131.80", {"start": v(45.23, -61.02) * mm, "end": v(45.23, -53.78) * mm});
            skLineSegment(sketch, "E131.81", {"start": v(45.23, -53.78) * mm, "end": v(46.67, -49.82) * mm});
            skLineSegment(sketch, "E131.82", {"start": v(46.67, -49.82) * mm, "end": v(48.06, -50.37) * mm});
            skLineSegment(sketch, "E131.83", {"start": v(48.06, -50.37) * mm, "end": v(49.1, -47.52) * mm});
            skLineSegment(sketch, "E131.84", {"start": v(49.1, -47.52) * mm, "end": v(47.7, -46.97) * mm});
            skLineSegment(sketch, "E131.85", {"start": v(47.7, -46.97) * mm, "end": v(52.02, -35.1) * mm});
            skLineSegment(sketch, "E131.86", {"start": v(52.02, -35.1) * mm, "end": v(53.44, -35.58) * mm});
            skLineSegment(sketch, "E131.87", {"start": v(53.44, -35.58) * mm, "end": v(54.48, -32.73) * mm});
            skLineSegment(sketch, "E131.88", {"start": v(54.48, -32.73) * mm, "end": v(53.05, -32.26) * mm});
            skLineSegment(sketch, "E131.89", {"start": v(53.05, -32.26) * mm, "end": v(55.78, -24.77) * mm});
            skLineSegment(sketch, "E131.90", {"start": v(55.78, -24.77) * mm, "end": v(60.42, -24.77) * mm});
            skLineSegment(sketch, "E131.91", {"start": v(60.42, -24.77) * mm, "end": v(60.42, -26.27) * mm});
            skLineSegment(sketch, "E131.92", {"start": v(60.42, -26.27) * mm, "end": v(63.45, -26.27) * mm});
            skLineSegment(sketch, "E131.93", {"start": v(63.45, -26.27) * mm, "end": v(63.45, -24.77) * mm});
            skLineSegment(sketch, "E131.94", {"start": v(63.45, -24.77) * mm, "end": v(70.17, -24.77) * mm});
            skLineSegment(sketch, "E131.95", {"start": v(70.17, -24.77) * mm, "end": v(70.17, -27.85) * mm});
            skLineSegment(sketch, "E131.96", {"start": v(70.17, -27.85) * mm, "end": v(80.2, -27.85) * mm});
            skLineSegment(sketch, "E131.97", {"start": v(80.2, -27.85) * mm, "end": v(80.2, -24.77) * mm});
            skLineSegment(sketch, "E131.98", {"start": v(80.2, -24.77) * mm, "end": v(88.21, -24.77) * mm});
            skLineSegment(sketch, "E131.99", {"start": v(88.21, -24.77) * mm, "end": v(88.21, -26.27) * mm});
            skLineSegment(sketch, "E131.100", {"start": v(88.21, -26.27) * mm, "end": v(91.14, -26.27) * mm});
            skLineSegment(sketch, "E131.101", {"start": v(91.14, -26.27) * mm, "end": v(91.14, -24.77) * mm});
            skLineSegment(sketch, "E131.102", {"start": v(91.14, -24.77) * mm, "end": v(96.03, -24.77) * mm});
            skLineSegment(sketch, "E131.103", {"start": v(96.03, -24.77) * mm, "end": v(98.7, -32.22) * mm});
            skLineSegment(sketch, "E131.104", {"start": v(98.7, -32.22) * mm, "end": v(97.3, -32.72) * mm});
            skLineSegment(sketch, "E131.105", {"start": v(97.3, -32.72) * mm, "end": v(98.32, -35.58) * mm});
            skLineSegment(sketch, "E131.106", {"start": v(42.05, -10.87) * mm, "end": v(44.16, -10.87) * mm});
            skLineSegment(sketch, "E131.107", {"start": v(98.32, -35.58) * mm, "end": v(99.73, -35.07) * mm});
            skLineSegment(sketch, "E131.108", {"start": v(99.73, -35.07) * mm, "end": v(104.02, -47.02) * mm});
            skLineSegment(sketch, "E131.109", {"start": v(104.02, -47.02) * mm, "end": v(102.61, -47.53) * mm});
            skLineSegment(sketch, "E131.110", {"start": v(102.61, -47.53) * mm, "end": v(103.64, -50.38) * mm});
            skLineSegment(sketch, "E131.111", {"start": v(103.64, -50.38) * mm, "end": v(105.05, -49.88) * mm});
            skLineSegment(sketch, "E131.112", {"start": v(105.05, -49.88) * mm, "end": v(106.5, -53.92) * mm});
            skLineSegment(sketch, "E131.113", {"start": v(106.5, -53.92) * mm, "end": v(106.5, -60.9) * mm});
            skLineSegment(sketch, "E131.114", {"start": v(106.5, -60.9) * mm, "end": v(110.1, -60.9) * mm});
            skLineSegment(sketch, "E131.115", {"start": v(110.1, -60.9) * mm, "end": v(110.1, -62.18) * mm});
            skLineSegment(sketch, "E131.116", {"start": v(110.1, -62.18) * mm, "end": v(113.14, -62.18) * mm});
            skLineSegment(sketch, "E131.117", {"start": v(113.14, -62.18) * mm, "end": v(113.14, -60.9) * mm});
            skLineSegment(sketch, "E131.118", {"start": v(113.14, -60.9) * mm, "end": v(125.77, -60.9) * mm});
            skLineSegment(sketch, "E131.119", {"start": v(125.77, -60.9) * mm, "end": v(125.77, -62.18) * mm});
            skLineSegment(sketch, "E131.120", {"start": v(125.77, -62.18) * mm, "end": v(128.8, -62.18) * mm});
            skLineSegment(sketch, "E131.121", {"start": v(128.8, -62.18) * mm, "end": v(128.8, -60.9) * mm});
            skLineSegment(sketch, "E131.122", {"start": v(128.8, -60.9) * mm, "end": v(132.74, -60.9) * mm});
            skLineSegment(sketch, "E131.123", {"start": v(132.74, -60.9) * mm, "end": v(132.74, -53.63) * mm});
            skLineSegment(sketch, "E131.124", {"start": v(132.74, -53.63) * mm, "end": v(134.01, -53.63) * mm});
            skLineSegment(sketch, "E131.125", {"start": v(134.01, -53.63) * mm, "end": v(134.01, -51.4) * mm});
            skLineSegment(sketch, "E131.126", {"start": v(134.01, -51.4) * mm, "end": v(132.74, -51.4) * mm});
            skSolve(sketch);
        }
        {
            var Q0;
            Q0=makeQuery(id+"F3.imprint","IMPRINT",FACE,{"disambiguationData":[TD([[makeQuery(id+"F3.imprint","IMPRINT",EDGE,{"derivedFrom":sQuery(id+"F3.wireOp",EDGE,"E131.0")}),-1.0]])]});
            extrude(context, id + "F4", {"entities" : qUnion([Q0]), "operationType" : NewBodyOperationType.ADD, "depth" : 0.25 * mm});
        }
        {
            var Q0;
            Q0=makeQuery(id+"F2.opExtrude","CAP_FACE",FACE,{"disambiguationData":[OSD([sQuery(id+"F0.wireOp",EDGE,"E107"),sQuery(id+"F0.wireOp",EDGE,"E108"),sQuery(id+"F0.wireOp",EDGE,"E125"),sQuery(id+"F0.wireOp",EDGE,"E127"),sQuery(id+"F0.wireOp",EDGE,"E128"),sQuery(id+"F0.wireOp",EDGE,"E129")])],"isStart":false});
            var sketch = newSketch(context, id + "F5", { "sketchPlane" : qUnion([Q0])});
            skLineSegment(sketch, "E132.0", {"start": v(43.65, -11.37) * mm, "end": v(37.3, -11.37) * mm});
            skLineSegment(sketch, "E132.1", {"start": v(43.65, -15.68) * mm, "end": v(43.65, -11.37) * mm});
            skLineSegment(sketch, "E132.2", {"start": v(37.3, -15.68) * mm, "end": v(43.65, -15.68) * mm});
            skArc(sketch, "E132.3", {"start": v(37.3, -11.37) * mm, "mid": v(35.15, -13.53) * mm, "end": v(37.3, -15.68) * mm});
            skSolve(sketch);
        }
        {
            var Q0;
            Q0=makeQuery(id+"F5.imprint","IMPRINT",FACE,{"disambiguationData":[TD([[makeQuery(id+"F5.imprint","IMPRINT",EDGE,{"derivedFrom":sQuery(id+"F5.wireOp",EDGE,"E132.0")}),-1.0]])]});
            extrude(context, id + "F6", {"entities" : qUnion([Q0]), "operationType" : NewBodyOperationType.ADD, "depth" : 0.25 * mm});
        }
        {
            var Q0;
            Q0=makeQuery(id+"F1.opExtrude","CAP_FACE",FACE,{"disambiguationData":[OSD([sQuery(id+"F0.wireOp",EDGE,"E0"),sQuery(id+"F0.wireOp",EDGE,"E1"),sQuery(id+"F0.wireOp",EDGE,"E2"),sQuery(id+"F0.wireOp",EDGE,"E3"),sQuery(id+"F0.wireOp",EDGE,"E4"),sQuery(id+"F0.wireOp",EDGE,"E5"),sQuery(id+"F0.wireOp",EDGE,"E6"),sQuery(id+"F0.wireOp",EDGE,"E7"),sQuery(id+"F0.wireOp",EDGE,"E8"),sQuery(id+"F0.wireOp",EDGE,"E9"),sQuery(id+"F0.wireOp",EDGE,"E10"),sQuery(id+"F0.wireOp",EDGE,"E11"),sQuery(id+"F0.wireOp",EDGE,"E12"),sQuery(id+"F0.wireOp",EDGE,"E13"),sQuery(id+"F0.wireOp",EDGE,"E14"),sQuery(id+"F0.wireOp",EDGE,"E15"),sQuery(id+"F0.wireOp",EDGE,"E16"),sQuery(id+"F0.wireOp",EDGE,"E17"),sQuery(id+"F0.wireOp",EDGE,"E18"),sQuery(id+"F0.wireOp",EDGE,"E19"),sQuery(id+"F0.wireOp",EDGE,"E20"),sQuery(id+"F0.wireOp",EDGE,"E21"),sQuery(id+"F0.wireOp",EDGE,"E22"),sQuery(id+"F0.wireOp",EDGE,"E23"),sQuery(id+"F0.wireOp",EDGE,"E24"),sQuery(id+"F0.wireOp",EDGE,"E25"),sQuery(id+"F0.wireOp",EDGE,"E26"),sQuery(id+"F0.wireOp",EDGE,"E27"),sQuery(id+"F0.wireOp",EDGE,"E28"),sQuery(id+"F0.wireOp",EDGE,"E29"),sQuery(id+"F0.wireOp",EDGE,"E30"),sQuery(id+"F0.wireOp",EDGE,"E31"),sQuery(id+"F0.wireOp",EDGE,"E32"),sQuery(id+"F0.wireOp",EDGE,"E33"),sQuery(id+"F0.wireOp",EDGE,"E34"),sQuery(id+"F0.wireOp",EDGE,"E35"),sQuery(id+"F0.wireOp",EDGE,"E36"),sQuery(id+"F0.wireOp",EDGE,"E37"),sQuery(id+"F0.wireOp",EDGE,"E38"),sQuery(id+"F0.wireOp",EDGE,"E39"),sQuery(id+"F0.wireOp",EDGE,"E40"),sQuery(id+"F0.wireOp",EDGE,"E41"),sQuery(id+"F0.wireOp",EDGE,"E42"),sQuery(id+"F0.wireOp",EDGE,"E43"),sQuery(id+"F0.wireOp",EDGE,"E44"),sQuery(id+"F0.wireOp",EDGE,"E45"),sQuery(id+"F0.wireOp",EDGE,"E46"),sQuery(id+"F0.wireOp",EDGE,"E47"),sQuery(id+"F0.wireOp",EDGE,"E48"),sQuery(id+"F0.wireOp",EDGE,"E49"),sQuery(id+"F0.wireOp",EDGE,"E50"),sQuery(id+"F0.wireOp",EDGE,"E51"),sQuery(id+"F0.wireOp",EDGE,"E52"),sQuery(id+"F0.wireOp",EDGE,"E53"),sQuery(id+"F0.wireOp",EDGE,"E54"),sQuery(id+"F0.wireOp",EDGE,"E55"),sQuery(id+"F0.wireOp",EDGE,"E56"),sQuery(id+"F0.wireOp",EDGE,"E57"),sQuery(id+"F0.wireOp",EDGE,"E58"),sQuery(id+"F0.wireOp",EDGE,"E59"),sQuery(id+"F0.wireOp",EDGE,"E60"),sQuery(id+"F0.wireOp",EDGE,"E61"),sQuery(id+"F0.wireOp",EDGE,"E62"),sQuery(id+"F0.wireOp",EDGE,"E63"),sQuery(id+"F0.wireOp",EDGE,"E64"),sQuery(id+"F0.wireOp",EDGE,"E65"),sQuery(id+"F0.wireOp",EDGE,"E66"),sQuery(id+"F0.wireOp",EDGE,"E67"),sQuery(id+"F0.wireOp",EDGE,"E68"),sQuery(id+"F0.wireOp",EDGE,"E69"),sQuery(id+"F0.wireOp",EDGE,"E70"),sQuery(id+"F0.wireOp",EDGE,"E71"),sQuery(id+"F0.wireOp",EDGE,"E72"),sQuery(id+"F0.wireOp",EDGE,"E73"),sQuery(id+"F0.wireOp",EDGE,"E74"),sQuery(id+"F0.wireOp",EDGE,"E75"),sQuery(id+"F0.wireOp",EDGE,"E76"),sQuery(id+"F0.wireOp",EDGE,"E77"),sQuery(id+"F0.wireOp",EDGE,"E78"),sQuery(id+"F0.wireOp",EDGE,"E79"),sQuery(id+"F0.wireOp",EDGE,"E80"),sQuery(id+"F0.wireOp",EDGE,"E81"),sQuery(id+"F0.wireOp",EDGE,"E82"),sQuery(id+"F0.wireOp",EDGE,"E83"),sQuery(id+"F0.wireOp",EDGE,"E84"),sQuery(id+"F0.wireOp",EDGE,"E85"),sQuery(id+"F0.wireOp",EDGE,"E86"),sQuery(id+"F0.wireOp",EDGE,"E87"),sQuery(id+"F0.wireOp",EDGE,"E88"),sQuery(id+"F0.wireOp",EDGE,"E89"),sQuery(id+"F0.wireOp",EDGE,"E90"),sQuery(id+"F0.wireOp",EDGE,"E91"),sQuery(id+"F0.wireOp",EDGE,"E92"),sQuery(id+"F0.wireOp",EDGE,"E93"),sQuery(id+"F0.wireOp",EDGE,"E94"),sQuery(id+"F0.wireOp",EDGE,"E95"),sQuery(id+"F0.wireOp",EDGE,"E96"),sQuery(id+"F0.wireOp",EDGE,"E97"),sQuery(id+"F0.wireOp",EDGE,"E98"),sQuery(id+"F0.wireOp",EDGE,"E99"),sQuery(id+"F0.wireOp",EDGE,"E100"),sQuery(id+"F0.wireOp",EDGE,"E101"),sQuery(id+"F0.wireOp",EDGE,"E102"),sQuery(id+"F0.wireOp",EDGE,"E103"),sQuery(id+"F0.wireOp",EDGE,"E104"),sQuery(id+"F0.wireOp",EDGE,"E105"),sQuery(id+"F0.wireOp",EDGE,"E106"),sQuery(id+"F0.wireOp",EDGE,"E107"),sQuery(id+"F0.wireOp",EDGE,"E108"),sQuery(id+"F0.wireOp",EDGE,"E109"),sQuery(id+"F0.wireOp",EDGE,"E110"),sQuery(id+"F0.wireOp",EDGE,"E111"),sQuery(id+"F0.wireOp",EDGE,"E112"),sQuery(id+"F0.wireOp",EDGE,"E113"),sQuery(id+"F0.wireOp",EDGE,"E114"),sQuery(id+"F0.wireOp",EDGE,"E115"),sQuery(id+"F0.wireOp",EDGE,"E116"),sQuery(id+"F0.wireOp",EDGE,"E117"),sQuery(id+"F0.wireOp",EDGE,"E118"),sQuery(id+"F0.wireOp",EDGE,"E119"),sQuery(id+"F0.wireOp",EDGE,"E120"),sQuery(id+"F0.wireOp",EDGE,"E121"),sQuery(id+"F0.wireOp",EDGE,"E122"),sQuery(id+"F0.wireOp",EDGE,"E123"),sQuery(id+"F0.wireOp",EDGE,"E124"),sQuery(id+"F0.wireOp",EDGE,"E125"),sQuery(id+"F0.wireOp",EDGE,"E126")])],"isStart":true});
            var sketch = newSketch(context, id + "F7", { "sketchPlane" : qUnion([Q0])});
            skLineSegment(sketch, "E133", {"start": v(4.3, 20.63) * mm, "end": v(41.79, 20.63) * mm});
            skSolve(sketch);
        }
        {
            var Q0;
            {var subQ5=makeQuery(id+"F1.opExtrude","CAP_EDGE",EDGE,{"disambiguationData":[OSD([sQuery(id+"F0.wireOp",EDGE,"E110")])],"isStart":true});Q0=makeQuery(id+"F7.imprint","IMPRINT",FACE,{"disambiguationData":[TD([[makeQuery(id+"F7.imprint","IMPRINT",EDGE,{"derivedFrom":subQ5}),1.0]])]});}
            extrude(context, id + "F8", {"entities" : qUnion([Q0]), "operationType" : NewBodyOperationType.ADD, "oppositeDirection" : true, "depth" : 3.56 * mm});
        }
        {
            var Q0;
            Q0=makeQuery(id+"F8.opExtrude","CAP_FACE",FACE,{"disambiguationData":[OSD([sQuery(id+"F0.wireOp",EDGE,"E109"),sQuery(id+"F0.wireOp",EDGE,"E110"),sQuery(id+"F0.wireOp",EDGE,"E111"),sQuery(id+"F0.wireOp",EDGE,"E112"),sQuery(id+"F0.wireOp",EDGE,"E113"),sQuery(id+"F0.wireOp",EDGE,"E114"),sQuery(id+"F0.wireOp",EDGE,"E115"),sQuery(id+"F0.wireOp",EDGE,"E116"),sQuery(id+"F0.wireOp",EDGE,"E117"),sQuery(id+"F0.wireOp",EDGE,"E118"),sQuery(id+"F0.wireOp",EDGE,"E119"),sQuery(id+"F0.wireOp",EDGE,"E120"),sQuery(id+"F0.wireOp",EDGE,"E121"),sQuery(id+"F0.wireOp",EDGE,"E122"),sQuery(id+"F7.wireOp",EDGE,"E133")])],"isStart":false});
            var sketch = newSketch(context, id + "F9", { "sketchPlane" : qUnion([Q0])});
            skLineSegment(sketch, "E134.bottom", {"start": v(20.04, -33.33) * mm, "end": v(31.65, -33.33) * mm});
            skLineSegment(sketch, "E134.top", {"start": v(20.04, -17.27) * mm, "end": v(31.65, -17.27) * mm});
            skLineSegment(sketch, "E134.left", {"start": v(20.04, -33.33) * mm, "end": v(20.04, -17.27) * mm});
            skLineSegment(sketch, "E134.right", {"start": v(31.65, -33.33) * mm, "end": v(31.65, -17.27) * mm});
            skLineSegment(sketch, "E135", {"start": v(25.84, -17.27) * mm, "end": v(25.84, -33.33) * mm, "construction": true});
            skSolve(sketch);
        }
        {
            var Q0;
            Q0=qSketchRegion(id+"F9",true);
            extrude(context, id + "F10", {"entities" : qUnion([Q0]), "operationType" : NewBodyOperationType.ADD, "depth" : 3.56 * mm});
        }
        {
            var Q0;
            {var subQ0=sQuery(id+"F0.wireOp",EDGE,"E122");var subQ1=sQuery(id+"F0.wireOp",EDGE,"E121");var subQ2=sQuery(id+"F0.wireOp",EDGE,"E120");var subQ3=sQuery(id+"F0.wireOp",EDGE,"E119");var subQ4=sQuery(id+"F0.wireOp",EDGE,"E118");var subQ5=sQuery(id+"F0.wireOp",EDGE,"E117");var subQ6=sQuery(id+"F0.wireOp",EDGE,"E116");var subQ7=sQuery(id+"F0.wireOp",EDGE,"E115");var subQ8=sQuery(id+"F0.wireOp",EDGE,"E114");var subQ9=sQuery(id+"F0.wireOp",EDGE,"E113");var subQ10=sQuery(id+"F0.wireOp",EDGE,"E112");var subQ11=sQuery(id+"F0.wireOp",EDGE,"E111");var subQ12=sQuery(id+"F0.wireOp",EDGE,"E110");var subQ13=sQuery(id+"F0.wireOp",EDGE,"E109");Q0=makeQuery(id+"F8.boolean.opBoolean","MERGE",FACE,{"derivedFrom":[makeQuery(id+"F1.opExtrude","CAP_FACE",FACE,{"disambiguationData":[OSD([sQuery(id+"F0.wireOp",EDGE,"E0"),sQuery(id+"F0.wireOp",EDGE,"E1"),sQuery(id+"F0.wireOp",EDGE,"E2"),sQuery(id+"F0.wireOp",EDGE,"E3"),sQuery(id+"F0.wireOp",EDGE,"E4"),sQuery(id+"F0.wireOp",EDGE,"E5"),sQuery(id+"F0.wireOp",EDGE,"E6"),sQuery(id+"F0.wireOp",EDGE,"E7"),sQuery(id+"F0.wireOp",EDGE,"E8"),sQuery(id+"F0.wireOp",EDGE,"E9"),sQuery(id+"F0.wireOp",EDGE,"E10"),sQuery(id+"F0.wireOp",EDGE,"E11"),sQuery(id+"F0.wireOp",EDGE,"E12"),sQuery(id+"F0.wireOp",EDGE,"E13"),sQuery(id+"F0.wireOp",EDGE,"E14"),sQuery(id+"F0.wireOp",EDGE,"E15"),sQuery(id+"F0.wireOp",EDGE,"E16"),sQuery(id+"F0.wireOp",EDGE,"E17"),sQuery(id+"F0.wireOp",EDGE,"E18"),sQuery(id+"F0.wireOp",EDGE,"E19"),sQuery(id+"F0.wireOp",EDGE,"E20"),sQuery(id+"F0.wireOp",EDGE,"E21"),sQuery(id+"F0.wireOp",EDGE,"E22"),sQuery(id+"F0.wireOp",EDGE,"E23"),sQuery(id+"F0.wireOp",EDGE,"E24"),sQuery(id+"F0.wireOp",EDGE,"E25"),sQuery(id+"F0.wireOp",EDGE,"E26"),sQuery(id+"F0.wireOp",EDGE,"E27"),sQuery(id+"F0.wireOp",EDGE,"E28"),sQuery(id+"F0.wireOp",EDGE,"E29"),sQuery(id+"F0.wireOp",EDGE,"E30"),sQuery(id+"F0.wireOp",EDGE,"E31"),sQuery(id+"F0.wireOp",EDGE,"E32"),sQuery(id+"F0.wireOp",EDGE,"E33"),sQuery(id+"F0.wireOp",EDGE,"E34"),sQuery(id+"F0.wireOp",EDGE,"E35"),sQuery(id+"F0.wireOp",EDGE,"E36"),sQuery(id+"F0.wireOp",EDGE,"E37"),sQuery(id+"F0.wireOp",EDGE,"E38"),sQuery(id+"F0.wireOp",EDGE,"E39"),sQuery(id+"F0.wireOp",EDGE,"E40"),sQuery(id+"F0.wireOp",EDGE,"E41"),sQuery(id+"F0.wireOp",EDGE,"E42"),sQuery(id+"F0.wireOp",EDGE,"E43"),sQuery(id+"F0.wireOp",EDGE,"E44"),sQuery(id+"F0.wireOp",EDGE,"E45"),sQuery(id+"F0.wireOp",EDGE,"E46"),sQuery(id+"F0.wireOp",EDGE,"E47"),sQuery(id+"F0.wireOp",EDGE,"E48"),sQuery(id+"F0.wireOp",EDGE,"E49"),sQuery(id+"F0.wireOp",EDGE,"E50"),sQuery(id+"F0.wireOp",EDGE,"E51"),sQuery(id+"F0.wireOp",EDGE,"E52"),sQuery(id+"F0.wireOp",EDGE,"E53"),sQuery(id+"F0.wireOp",EDGE,"E54"),sQuery(id+"F0.wireOp",EDGE,"E55"),sQuery(id+"F0.wireOp",EDGE,"E56"),sQuery(id+"F0.wireOp",EDGE,"E57"),sQuery(id+"F0.wireOp",EDGE,"E58"),sQuery(id+"F0.wireOp",EDGE,"E59"),sQuery(id+"F0.wireOp",EDGE,"E60"),sQuery(id+"F0.wireOp",EDGE,"E61"),sQuery(id+"F0.wireOp",EDGE,"E62"),sQuery(id+"F0.wireOp",EDGE,"E63"),sQuery(id+"F0.wireOp",EDGE,"E64"),sQuery(id+"F0.wireOp",EDGE,"E65"),sQuery(id+"F0.wireOp",EDGE,"E66"),sQuery(id+"F0.wireOp",EDGE,"E67"),sQuery(id+"F0.wireOp",EDGE,"E68"),sQuery(id+"F0.wireOp",EDGE,"E69"),sQuery(id+"F0.wireOp",EDGE,"E70"),sQuery(id+"F0.wireOp",EDGE,"E71"),sQuery(id+"F0.wireOp",EDGE,"E72"),sQuery(id+"F0.wireOp",EDGE,"E73"),sQuery(id+"F0.wireOp",EDGE,"E74"),sQuery(id+"F0.wireOp",EDGE,"E75"),sQuery(id+"F0.wireOp",EDGE,"E76"),sQuery(id+"F0.wireOp",EDGE,"E77"),sQuery(id+"F0.wireOp",EDGE,"E78"),sQuery(id+"F0.wireOp",EDGE,"E79"),sQuery(id+"F0.wireOp",EDGE,"E80"),sQuery(id+"F0.wireOp",EDGE,"E81"),sQuery(id+"F0.wireOp",EDGE,"E82"),sQuery(id+"F0.wireOp",EDGE,"E83"),sQuery(id+"F0.wireOp",EDGE,"E84"),sQuery(id+"F0.wireOp",EDGE,"E85"),sQuery(id+"F0.wireOp",EDGE,"E86"),sQuery(id+"F0.wireOp",EDGE,"E87"),sQuery(id+"F0.wireOp",EDGE,"E88"),sQuery(id+"F0.wireOp",EDGE,"E89"),sQuery(id+"F0.wireOp",EDGE,"E90"),sQuery(id+"F0.wireOp",EDGE,"E91"),sQuery(id+"F0.wireOp",EDGE,"E92"),sQuery(id+"F0.wireOp",EDGE,"E93"),sQuery(id+"F0.wireOp",EDGE,"E94"),sQuery(id+"F0.wireOp",EDGE,"E95"),sQuery(id+"F0.wireOp",EDGE,"E96"),sQuery(id+"F0.wireOp",EDGE,"E97"),sQuery(id+"F0.wireOp",EDGE,"E98"),sQuery(id+"F0.wireOp",EDGE,"E99"),sQuery(id+"F0.wireOp",EDGE,"E100"),sQuery(id+"F0.wireOp",EDGE,"E101"),sQuery(id+"F0.wireOp",EDGE,"E102"),sQuery(id+"F0.wireOp",EDGE,"E103"),sQuery(id+"F0.wireOp",EDGE,"E104"),sQuery(id+"F0.wireOp",EDGE,"E105"),sQuery(id+"F0.wireOp",EDGE,"E106"),sQuery(id+"F0.wireOp",EDGE,"E107"),sQuery(id+"F0.wireOp",EDGE,"E108"),subQ13,subQ12,subQ11,subQ10,subQ9,subQ8,subQ7,subQ6,subQ5,subQ4,subQ3,subQ2,subQ1,subQ0,sQuery(id+"F0.wireOp",EDGE,"E123"),sQuery(id+"F0.wireOp",EDGE,"E124"),sQuery(id+"F0.wireOp",EDGE,"E125"),sQuery(id+"F0.wireOp",EDGE,"E126")])],"isStart":true}),makeQuery(id+"F8.opExtrude","CAP_FACE",FACE,{"disambiguationData":[OSD([subQ13,subQ12,subQ11,subQ10,subQ9,subQ8,subQ7,subQ6,subQ5,subQ4,subQ3,subQ2,subQ1,subQ0,sQuery(id+"F7.wireOp",EDGE,"E133")])],"isStart":true})]});}
            var sketch = newSketch(context, id + "F11", { "sketchPlane" : qUnion([Q0])});
            skLineSegment(sketch, "E136.bottom", {"start": v(9.31, 61.28) * mm, "end": v(41.38, 61.28) * mm});
            skLineSegment(sketch, "E136.top", {"start": v(9.31, 66.14) * mm, "end": v(41.38, 66.14) * mm});
            skLineSegment(sketch, "E136.left", {"start": v(9.31, 61.28) * mm, "end": v(9.31, 66.14) * mm});
            skLineSegment(sketch, "E136.right", {"start": v(41.38, 61.28) * mm, "end": v(41.38, 66.14) * mm});
            skLineSegment(sketch, "E137.bottom", {"start": v(108.05, 61.16) * mm, "end": v(133.42, 61.16) * mm});
            skLineSegment(sketch, "E137.top", {"start": v(108.05, 72.36) * mm, "end": v(133.42, 72.36) * mm});
            skLineSegment(sketch, "E137.left", {"start": v(108.05, 61.16) * mm, "end": v(108.05, 72.36) * mm});
            skLineSegment(sketch, "E137.right", {"start": v(133.42, 61.16) * mm, "end": v(133.42, 72.36) * mm});
            skLineSegment(sketch, "E138", {"start": v(5.43, 51.48) * mm, "end": v(-1.66, 28.28) * mm});
            skLineSegment(sketch, "E139", {"start": v(-1.66, 28.28) * mm, "end": v(-10.07, 37.62) * mm});
            skLineSegment(sketch, "E140", {"start": v(-10.07, 37.62) * mm, "end": v(1.62, 52.12) * mm});
            skLineSegment(sketch, "E141", {"start": v(1.62, 52.12) * mm, "end": v(5.43, 51.48) * mm});
            skLineSegment(sketch, "E142.bottom", {"start": v(80.46, 25.02) * mm, "end": v(66.83, 25.02) * mm});
            skLineSegment(sketch, "E142.top", {"start": v(80.46, 28.5) * mm, "end": v(66.83, 28.5) * mm});
            skLineSegment(sketch, "E142.left", {"start": v(80.46, 25.02) * mm, "end": v(80.46, 28.5) * mm});
            skLineSegment(sketch, "E142.right", {"start": v(66.83, 25.02) * mm, "end": v(66.83, 28.5) * mm});
            skLineSegment(sketch, "E143", {"start": v(54.25, 29.71) * mm, "end": v(97.5, 29.6) * mm});
            skLineSegment(sketch, "E144", {"start": v(97.5, 29.6) * mm, "end": v(105.57, 52.08) * mm});
            skLineSegment(sketch, "E145", {"start": v(105.57, 52.08) * mm, "end": v(46.12, 52.08) * mm});
            skLineSegment(sketch, "E146", {"start": v(46.12, 52.08) * mm, "end": v(54.25, 29.71) * mm});
            skLineSegment(sketch, "E147.bottom", {"start": v(134.26, 53.89) * mm, "end": v(133, 53.89) * mm});
            skLineSegment(sketch, "E147.top", {"start": v(134.26, 47.34) * mm, "end": v(133, 47.34) * mm});
            skLineSegment(sketch, "E147.left", {"start": v(134.26, 53.89) * mm, "end": v(134.26, 47.34) * mm});
            skLineSegment(sketch, "E147.right", {"start": v(133, 53.89) * mm, "end": v(133, 47.34) * mm});
            skLineSegment(sketch, "E148.bottom", {"start": v(106.47, 2.03) * mm, "end": v(95.07, 2.03) * mm});
            skLineSegment(sketch, "E148.top", {"start": v(106.47, 4.25) * mm, "end": v(95.07, 4.25) * mm});
            skLineSegment(sketch, "E148.left", {"start": v(106.47, 2.03) * mm, "end": v(106.47, 4.25) * mm});
            skLineSegment(sketch, "E148.right", {"start": v(95.07, 2.03) * mm, "end": v(95.07, 4.25) * mm});
            skLineSegment(sketch, "E149.bottom", {"start": v(52.93, 4.25) * mm, "end": v(44.68, 4.25) * mm});
            skLineSegment(sketch, "E149.top", {"start": v(52.93, 2.03) * mm, "end": v(44.68, 2.03) * mm});
            skLineSegment(sketch, "E149.left", {"start": v(52.93, 4.25) * mm, "end": v(52.93, 2.03) * mm});
            skLineSegment(sketch, "E149.right", {"start": v(44.68, 4.25) * mm, "end": v(44.68, 2.03) * mm});
            skLineSegment(sketch, "E150.bottom", {"start": v(0, 0) * mm, "end": v(8.5, 0) * mm});
            skLineSegment(sketch, "E150.top", {"start": v(0, 2.24) * mm, "end": v(8.5, 2.24) * mm});
            skLineSegment(sketch, "E150.left", {"start": v(0, 0) * mm, "end": v(0, 2.24) * mm});
            skLineSegment(sketch, "E150.right", {"start": v(8.5, 0) * mm, "end": v(8.5, 2.24) * mm});
            skLineSegment(sketch, "E151", {"start": v(108.85, 23.13) * mm, "end": v(108.85, 13.22) * mm});
            skLineSegment(sketch, "E152", {"start": v(108.85, 13.22) * mm, "end": v(112.92, 10.07) * mm});
            skLineSegment(sketch, "E153", {"start": v(112.92, 10.07) * mm, "end": v(114, 25.99) * mm});
            skLineSegment(sketch, "E154", {"start": v(114, 25.99) * mm, "end": v(108.85, 23.13) * mm});
            skLineSegment(sketch, "E155", {"start": v(-3.01, 18.02) * mm, "end": v(-3.01, 23.84) * mm});
            skLineSegment(sketch, "E156", {"start": v(-3.01, 23.84) * mm, "end": v(-9.3, 26.77) * mm});
            skLineSegment(sketch, "E157", {"start": v(-9.3, 26.77) * mm, "end": v(-7.64, 16.15) * mm});
            skLineSegment(sketch, "E158", {"start": v(-7.64, 16.15) * mm, "end": v(-3.01, 18.02) * mm});
            skSolve(sketch);
        }
        {
            var Q0;
            Q0=qSketchRegion(id+"F11",true);
            extrude(context, id + "F12", {"entities" : qUnion([Q0]), "operationType" : NewBodyOperationType.REMOVE, "oppositeDirection" : true, "depth" : 3.56 * mm});
        }
        {
            var Q0;
            {var subQ0=sQuery(id+"F9.wireOp",EDGE,"E134.left");var subQ1=sQuery(id+"F9.wireOp",EDGE,"E134.right");var subQ2=sQuery(id+"F7.wireOp",EDGE,"E133");var subQ3=sQuery(id+"F0.wireOp",EDGE,"E109");var subQ4=makeQuery(id+"F8.opExtrude","CAP_FACE",FACE,{"disambiguationData":[OSD([subQ3,sQuery(id+"F0.wireOp",EDGE,"E110"),sQuery(id+"F0.wireOp",EDGE,"E111"),sQuery(id+"F0.wireOp",EDGE,"E112"),sQuery(id+"F0.wireOp",EDGE,"E113"),sQuery(id+"F0.wireOp",EDGE,"E114"),sQuery(id+"F0.wireOp",EDGE,"E115"),sQuery(id+"F0.wireOp",EDGE,"E116"),sQuery(id+"F0.wireOp",EDGE,"E117"),sQuery(id+"F0.wireOp",EDGE,"E118"),sQuery(id+"F0.wireOp",EDGE,"E119"),sQuery(id+"F0.wireOp",EDGE,"E120"),sQuery(id+"F0.wireOp",EDGE,"E121"),sQuery(id+"F0.wireOp",EDGE,"E122"),subQ2])],"isStart":false});var subQ5=makeQuery(id+"F8.opExtrude","SWEPT_FACE",FACE,{"disambiguationData":[OSD([subQ2])]});Q0=makeQuery(id+"F10.boolean.opBoolean","SPLIT",EDGE,{"disambiguationData":[TD([subQ5,subQ4,makeQuery(id+"F10.opExtrude","CAP_FACE",FACE,{"disambiguationData":[OSD([sQuery(id+"F9.wireOp",EDGE,"E134.bottom"),sQuery(id+"F9.wireOp",EDGE,"E134.top"),subQ0,subQ1])],"isStart":true}),makeQuery(id+"F10.opExtrude","SWEPT_FACE",FACE,{"disambiguationData":[OSD([subQ0])]}),makeQuery(id+"F10.opExtrude","SWEPT_FACE",FACE,{"disambiguationData":[OSD([subQ1])]})])],"derivedFrom":makeQuery(id+"F8.boolean.opBoolean","SPLIT",EDGE,{"disambiguationData":[TD([makeQuery(id+"F1.opExtrude","SWEPT_FACE",FACE,{"disambiguationData":[OSD([subQ3])]})])],"derivedFrom":makeQuery(id+"F8.opExtrude","CAP_EDGE",EDGE,{"disambiguationData":[OSD([subQ2])],"isStart":false})})});}
            fillet(context, id + "F13", {"entities" : qUnion([Q0]), "radius" : 1.27 * mm, "tangentPropagation" : true, "allowEdgeOverflow" : false});
        }
        {
            var Q0;
            {var subQ0=sQuery(id+"F9.wireOp",EDGE,"E134.left");var subQ1=sQuery(id+"F9.wireOp",EDGE,"E134.bottom");Q0=makeQuery(id+"F10.boolean.opBoolean","SPLIT",EDGE,{"disambiguationData":[TD([makeQuery(id+"F10.opExtrude","SWEPT_FACE",FACE,{"disambiguationData":[OSD([subQ1])]})])],"derivedFrom":makeQuery(id+"F10.opExtrude","CAP_EDGE",EDGE,{"disambiguationData":[OSD([subQ0])],"isStart":true})});}
            var Q1;
            Q1=makeQuery(id+"F10.opExtrude","CAP_EDGE",EDGE,{"disambiguationData":[OSD([sQuery(id+"F9.wireOp",EDGE,"E134.bottom")])],"isStart":true});
            var Q2;
            {var subQ0=sQuery(id+"F9.wireOp",EDGE,"E134.right");var subQ1=sQuery(id+"F9.wireOp",EDGE,"E134.bottom");Q2=makeQuery(id+"F10.boolean.opBoolean","SPLIT",EDGE,{"disambiguationData":[TD([makeQuery(id+"F10.opExtrude","SWEPT_FACE",FACE,{"disambiguationData":[OSD([subQ1])]})])],"derivedFrom":makeQuery(id+"F10.opExtrude","CAP_EDGE",EDGE,{"disambiguationData":[OSD([subQ0])],"isStart":true})});}
            fillet(context, id + "F14", {"entities" : qUnion([Q0, Q1, Q2]), "radius" : 0.25 * mm, "tangentPropagation" : true, "allowEdgeOverflow" : false});
        }
        {
            var Q0;
            {var subQ0=sQuery(id+"F0.wireOp",EDGE,"E122");var subQ1=sQuery(id+"F0.wireOp",EDGE,"E121");var subQ2=sQuery(id+"F0.wireOp",EDGE,"E120");var subQ3=sQuery(id+"F0.wireOp",EDGE,"E119");var subQ4=sQuery(id+"F0.wireOp",EDGE,"E118");var subQ5=sQuery(id+"F0.wireOp",EDGE,"E117");var subQ6=sQuery(id+"F0.wireOp",EDGE,"E116");var subQ7=sQuery(id+"F0.wireOp",EDGE,"E115");var subQ8=sQuery(id+"F0.wireOp",EDGE,"E114");var subQ9=sQuery(id+"F0.wireOp",EDGE,"E113");var subQ10=sQuery(id+"F0.wireOp",EDGE,"E112");var subQ11=sQuery(id+"F0.wireOp",EDGE,"E111");var subQ12=sQuery(id+"F0.wireOp",EDGE,"E110");var subQ13=sQuery(id+"F0.wireOp",EDGE,"E109");Q0=makeQuery(id+"F8.boolean.opBoolean","MERGE",FACE,{"derivedFrom":[makeQuery(id+"F1.opExtrude","CAP_FACE",FACE,{"disambiguationData":[OSD([sQuery(id+"F0.wireOp",EDGE,"E0"),sQuery(id+"F0.wireOp",EDGE,"E1"),sQuery(id+"F0.wireOp",EDGE,"E2"),sQuery(id+"F0.wireOp",EDGE,"E3"),sQuery(id+"F0.wireOp",EDGE,"E4"),sQuery(id+"F0.wireOp",EDGE,"E5"),sQuery(id+"F0.wireOp",EDGE,"E6"),sQuery(id+"F0.wireOp",EDGE,"E7"),sQuery(id+"F0.wireOp",EDGE,"E8"),sQuery(id+"F0.wireOp",EDGE,"E9"),sQuery(id+"F0.wireOp",EDGE,"E10"),sQuery(id+"F0.wireOp",EDGE,"E11"),sQuery(id+"F0.wireOp",EDGE,"E12"),sQuery(id+"F0.wireOp",EDGE,"E13"),sQuery(id+"F0.wireOp",EDGE,"E14"),sQuery(id+"F0.wireOp",EDGE,"E15"),sQuery(id+"F0.wireOp",EDGE,"E16"),sQuery(id+"F0.wireOp",EDGE,"E17"),sQuery(id+"F0.wireOp",EDGE,"E18"),sQuery(id+"F0.wireOp",EDGE,"E19"),sQuery(id+"F0.wireOp",EDGE,"E20"),sQuery(id+"F0.wireOp",EDGE,"E21"),sQuery(id+"F0.wireOp",EDGE,"E22"),sQuery(id+"F0.wireOp",EDGE,"E23"),sQuery(id+"F0.wireOp",EDGE,"E24"),sQuery(id+"F0.wireOp",EDGE,"E25"),sQuery(id+"F0.wireOp",EDGE,"E26"),sQuery(id+"F0.wireOp",EDGE,"E27"),sQuery(id+"F0.wireOp",EDGE,"E28"),sQuery(id+"F0.wireOp",EDGE,"E29"),sQuery(id+"F0.wireOp",EDGE,"E30"),sQuery(id+"F0.wireOp",EDGE,"E31"),sQuery(id+"F0.wireOp",EDGE,"E32"),sQuery(id+"F0.wireOp",EDGE,"E33"),sQuery(id+"F0.wireOp",EDGE,"E34"),sQuery(id+"F0.wireOp",EDGE,"E35"),sQuery(id+"F0.wireOp",EDGE,"E36"),sQuery(id+"F0.wireOp",EDGE,"E37"),sQuery(id+"F0.wireOp",EDGE,"E38"),sQuery(id+"F0.wireOp",EDGE,"E39"),sQuery(id+"F0.wireOp",EDGE,"E40"),sQuery(id+"F0.wireOp",EDGE,"E41"),sQuery(id+"F0.wireOp",EDGE,"E42"),sQuery(id+"F0.wireOp",EDGE,"E43"),sQuery(id+"F0.wireOp",EDGE,"E44"),sQuery(id+"F0.wireOp",EDGE,"E45"),sQuery(id+"F0.wireOp",EDGE,"E46"),sQuery(id+"F0.wireOp",EDGE,"E47"),sQuery(id+"F0.wireOp",EDGE,"E48"),sQuery(id+"F0.wireOp",EDGE,"E49"),sQuery(id+"F0.wireOp",EDGE,"E50"),sQuery(id+"F0.wireOp",EDGE,"E51"),sQuery(id+"F0.wireOp",EDGE,"E52"),sQuery(id+"F0.wireOp",EDGE,"E53"),sQuery(id+"F0.wireOp",EDGE,"E54"),sQuery(id+"F0.wireOp",EDGE,"E55"),sQuery(id+"F0.wireOp",EDGE,"E56"),sQuery(id+"F0.wireOp",EDGE,"E57"),sQuery(id+"F0.wireOp",EDGE,"E58"),sQuery(id+"F0.wireOp",EDGE,"E59"),sQuery(id+"F0.wireOp",EDGE,"E60"),sQuery(id+"F0.wireOp",EDGE,"E61"),sQuery(id+"F0.wireOp",EDGE,"E62"),sQuery(id+"F0.wireOp",EDGE,"E63"),sQuery(id+"F0.wireOp",EDGE,"E64"),sQuery(id+"F0.wireOp",EDGE,"E65"),sQuery(id+"F0.wireOp",EDGE,"E66"),sQuery(id+"F0.wireOp",EDGE,"E67"),sQuery(id+"F0.wireOp",EDGE,"E68"),sQuery(id+"F0.wireOp",EDGE,"E69"),sQuery(id+"F0.wireOp",EDGE,"E70"),sQuery(id+"F0.wireOp",EDGE,"E71"),sQuery(id+"F0.wireOp",EDGE,"E72"),sQuery(id+"F0.wireOp",EDGE,"E73"),sQuery(id+"F0.wireOp",EDGE,"E74"),sQuery(id+"F0.wireOp",EDGE,"E75"),sQuery(id+"F0.wireOp",EDGE,"E76"),sQuery(id+"F0.wireOp",EDGE,"E77"),sQuery(id+"F0.wireOp",EDGE,"E78"),sQuery(id+"F0.wireOp",EDGE,"E79"),sQuery(id+"F0.wireOp",EDGE,"E80"),sQuery(id+"F0.wireOp",EDGE,"E81"),sQuery(id+"F0.wireOp",EDGE,"E82"),sQuery(id+"F0.wireOp",EDGE,"E83"),sQuery(id+"F0.wireOp",EDGE,"E84"),sQuery(id+"F0.wireOp",EDGE,"E85"),sQuery(id+"F0.wireOp",EDGE,"E86"),sQuery(id+"F0.wireOp",EDGE,"E87"),sQuery(id+"F0.wireOp",EDGE,"E88"),sQuery(id+"F0.wireOp",EDGE,"E89"),sQuery(id+"F0.wireOp",EDGE,"E90"),sQuery(id+"F0.wireOp",EDGE,"E91"),sQuery(id+"F0.wireOp",EDGE,"E92"),sQuery(id+"F0.wireOp",EDGE,"E93"),sQuery(id+"F0.wireOp",EDGE,"E94"),sQuery(id+"F0.wireOp",EDGE,"E95"),sQuery(id+"F0.wireOp",EDGE,"E96"),sQuery(id+"F0.wireOp",EDGE,"E97"),sQuery(id+"F0.wireOp",EDGE,"E98"),sQuery(id+"F0.wireOp",EDGE,"E99"),sQuery(id+"F0.wireOp",EDGE,"E100"),sQuery(id+"F0.wireOp",EDGE,"E101"),sQuery(id+"F0.wireOp",EDGE,"E102"),sQuery(id+"F0.wireOp",EDGE,"E103"),sQuery(id+"F0.wireOp",EDGE,"E104"),sQuery(id+"F0.wireOp",EDGE,"E105"),sQuery(id+"F0.wireOp",EDGE,"E106"),sQuery(id+"F0.wireOp",EDGE,"E107"),sQuery(id+"F0.wireOp",EDGE,"E108"),subQ13,subQ12,subQ11,subQ10,subQ9,subQ8,subQ7,subQ6,subQ5,subQ4,subQ3,subQ2,subQ1,subQ0,sQuery(id+"F0.wireOp",EDGE,"E123"),sQuery(id+"F0.wireOp",EDGE,"E124"),sQuery(id+"F0.wireOp",EDGE,"E125"),sQuery(id+"F0.wireOp",EDGE,"E126")])],"isStart":true}),makeQuery(id+"F8.opExtrude","CAP_FACE",FACE,{"disambiguationData":[OSD([subQ13,subQ12,subQ11,subQ10,subQ9,subQ8,subQ7,subQ6,subQ5,subQ4,subQ3,subQ2,subQ1,subQ0,sQuery(id+"F7.wireOp",EDGE,"E133")])],"isStart":true})]});}
            var sketch = newSketch(context, id + "F15", { "sketchPlane" : qUnion([Q0])});
            skLineSegment(sketch, "E159.bottom", {"start": v(80.46, 13.22) * mm, "end": v(69.91, 13.22) * mm});
            skLineSegment(sketch, "E159.top", {"start": v(80.46, 10.66) * mm, "end": v(69.91, 10.66) * mm});
            skLineSegment(sketch, "E159.left", {"start": v(80.46, 13.22) * mm, "end": v(80.46, 10.66) * mm});
            skLineSegment(sketch, "E159.right", {"start": v(69.91, 13.22) * mm, "end": v(69.91, 10.66) * mm});
            skSolve(sketch);
        }
        {
            var Q0;
            Q0=qSketchRegion(id+"F15",true);
            extrude(context, id + "F16", {"entities" : qUnion([Q0]), "operationType" : NewBodyOperationType.REMOVE, "oppositeDirection" : true, "depth" : 6.35 * mm});
        }
        {
            var Q0;
            {var subQ0=sQuery(id+"F0.wireOp",EDGE,"E122");var subQ1=sQuery(id+"F0.wireOp",EDGE,"E121");var subQ2=sQuery(id+"F0.wireOp",EDGE,"E120");var subQ3=sQuery(id+"F0.wireOp",EDGE,"E119");var subQ4=sQuery(id+"F0.wireOp",EDGE,"E118");var subQ5=sQuery(id+"F0.wireOp",EDGE,"E117");var subQ6=sQuery(id+"F0.wireOp",EDGE,"E116");var subQ7=sQuery(id+"F0.wireOp",EDGE,"E115");var subQ8=sQuery(id+"F0.wireOp",EDGE,"E114");var subQ9=sQuery(id+"F0.wireOp",EDGE,"E113");var subQ10=sQuery(id+"F0.wireOp",EDGE,"E112");var subQ11=sQuery(id+"F0.wireOp",EDGE,"E111");var subQ12=sQuery(id+"F0.wireOp",EDGE,"E110");var subQ13=sQuery(id+"F0.wireOp",EDGE,"E109");Q0=makeQuery(id+"F8.boolean.opBoolean","MERGE",FACE,{"derivedFrom":[makeQuery(id+"F1.opExtrude","CAP_FACE",FACE,{"disambiguationData":[OSD([sQuery(id+"F0.wireOp",EDGE,"E0"),sQuery(id+"F0.wireOp",EDGE,"E1"),sQuery(id+"F0.wireOp",EDGE,"E2"),sQuery(id+"F0.wireOp",EDGE,"E3"),sQuery(id+"F0.wireOp",EDGE,"E4"),sQuery(id+"F0.wireOp",EDGE,"E5"),sQuery(id+"F0.wireOp",EDGE,"E6"),sQuery(id+"F0.wireOp",EDGE,"E7"),sQuery(id+"F0.wireOp",EDGE,"E8"),sQuery(id+"F0.wireOp",EDGE,"E9"),sQuery(id+"F0.wireOp",EDGE,"E10"),sQuery(id+"F0.wireOp",EDGE,"E11"),sQuery(id+"F0.wireOp",EDGE,"E12"),sQuery(id+"F0.wireOp",EDGE,"E13"),sQuery(id+"F0.wireOp",EDGE,"E14"),sQuery(id+"F0.wireOp",EDGE,"E15"),sQuery(id+"F0.wireOp",EDGE,"E16"),sQuery(id+"F0.wireOp",EDGE,"E17"),sQuery(id+"F0.wireOp",EDGE,"E18"),sQuery(id+"F0.wireOp",EDGE,"E19"),sQuery(id+"F0.wireOp",EDGE,"E20"),sQuery(id+"F0.wireOp",EDGE,"E21"),sQuery(id+"F0.wireOp",EDGE,"E22"),sQuery(id+"F0.wireOp",EDGE,"E23"),sQuery(id+"F0.wireOp",EDGE,"E24"),sQuery(id+"F0.wireOp",EDGE,"E25"),sQuery(id+"F0.wireOp",EDGE,"E26"),sQuery(id+"F0.wireOp",EDGE,"E27"),sQuery(id+"F0.wireOp",EDGE,"E28"),sQuery(id+"F0.wireOp",EDGE,"E29"),sQuery(id+"F0.wireOp",EDGE,"E30"),sQuery(id+"F0.wireOp",EDGE,"E31"),sQuery(id+"F0.wireOp",EDGE,"E32"),sQuery(id+"F0.wireOp",EDGE,"E33"),sQuery(id+"F0.wireOp",EDGE,"E34"),sQuery(id+"F0.wireOp",EDGE,"E35"),sQuery(id+"F0.wireOp",EDGE,"E36"),sQuery(id+"F0.wireOp",EDGE,"E37"),sQuery(id+"F0.wireOp",EDGE,"E38"),sQuery(id+"F0.wireOp",EDGE,"E39"),sQuery(id+"F0.wireOp",EDGE,"E40"),sQuery(id+"F0.wireOp",EDGE,"E41"),sQuery(id+"F0.wireOp",EDGE,"E42"),sQuery(id+"F0.wireOp",EDGE,"E43"),sQuery(id+"F0.wireOp",EDGE,"E44"),sQuery(id+"F0.wireOp",EDGE,"E45"),sQuery(id+"F0.wireOp",EDGE,"E46"),sQuery(id+"F0.wireOp",EDGE,"E47"),sQuery(id+"F0.wireOp",EDGE,"E48"),sQuery(id+"F0.wireOp",EDGE,"E49"),sQuery(id+"F0.wireOp",EDGE,"E50"),sQuery(id+"F0.wireOp",EDGE,"E51"),sQuery(id+"F0.wireOp",EDGE,"E52"),sQuery(id+"F0.wireOp",EDGE,"E53"),sQuery(id+"F0.wireOp",EDGE,"E54"),sQuery(id+"F0.wireOp",EDGE,"E55"),sQuery(id+"F0.wireOp",EDGE,"E56"),sQuery(id+"F0.wireOp",EDGE,"E57"),sQuery(id+"F0.wireOp",EDGE,"E58"),sQuery(id+"F0.wireOp",EDGE,"E59"),sQuery(id+"F0.wireOp",EDGE,"E60"),sQuery(id+"F0.wireOp",EDGE,"E61"),sQuery(id+"F0.wireOp",EDGE,"E62"),sQuery(id+"F0.wireOp",EDGE,"E63"),sQuery(id+"F0.wireOp",EDGE,"E64"),sQuery(id+"F0.wireOp",EDGE,"E65"),sQuery(id+"F0.wireOp",EDGE,"E66"),sQuery(id+"F0.wireOp",EDGE,"E67"),sQuery(id+"F0.wireOp",EDGE,"E68"),sQuery(id+"F0.wireOp",EDGE,"E69"),sQuery(id+"F0.wireOp",EDGE,"E70"),sQuery(id+"F0.wireOp",EDGE,"E71"),sQuery(id+"F0.wireOp",EDGE,"E72"),sQuery(id+"F0.wireOp",EDGE,"E73"),sQuery(id+"F0.wireOp",EDGE,"E74"),sQuery(id+"F0.wireOp",EDGE,"E75"),sQuery(id+"F0.wireOp",EDGE,"E76"),sQuery(id+"F0.wireOp",EDGE,"E77"),sQuery(id+"F0.wireOp",EDGE,"E78"),sQuery(id+"F0.wireOp",EDGE,"E79"),sQuery(id+"F0.wireOp",EDGE,"E80"),sQuery(id+"F0.wireOp",EDGE,"E81"),sQuery(id+"F0.wireOp",EDGE,"E82"),sQuery(id+"F0.wireOp",EDGE,"E83"),sQuery(id+"F0.wireOp",EDGE,"E84"),sQuery(id+"F0.wireOp",EDGE,"E85"),sQuery(id+"F0.wireOp",EDGE,"E86"),sQuery(id+"F0.wireOp",EDGE,"E87"),sQuery(id+"F0.wireOp",EDGE,"E88"),sQuery(id+"F0.wireOp",EDGE,"E89"),sQuery(id+"F0.wireOp",EDGE,"E90"),sQuery(id+"F0.wireOp",EDGE,"E91"),sQuery(id+"F0.wireOp",EDGE,"E92"),sQuery(id+"F0.wireOp",EDGE,"E93"),sQuery(id+"F0.wireOp",EDGE,"E94"),sQuery(id+"F0.wireOp",EDGE,"E95"),sQuery(id+"F0.wireOp",EDGE,"E96"),sQuery(id+"F0.wireOp",EDGE,"E97"),sQuery(id+"F0.wireOp",EDGE,"E98"),sQuery(id+"F0.wireOp",EDGE,"E99"),sQuery(id+"F0.wireOp",EDGE,"E100"),sQuery(id+"F0.wireOp",EDGE,"E101"),sQuery(id+"F0.wireOp",EDGE,"E102"),sQuery(id+"F0.wireOp",EDGE,"E103"),sQuery(id+"F0.wireOp",EDGE,"E104"),sQuery(id+"F0.wireOp",EDGE,"E105"),sQuery(id+"F0.wireOp",EDGE,"E106"),sQuery(id+"F0.wireOp",EDGE,"E107"),sQuery(id+"F0.wireOp",EDGE,"E108"),subQ13,subQ12,subQ11,subQ10,subQ9,subQ8,subQ7,subQ6,subQ5,subQ4,subQ3,subQ2,subQ1,subQ0,sQuery(id+"F0.wireOp",EDGE,"E123"),sQuery(id+"F0.wireOp",EDGE,"E124"),sQuery(id+"F0.wireOp",EDGE,"E125"),sQuery(id+"F0.wireOp",EDGE,"E126")])],"isStart":true}),makeQuery(id+"F8.opExtrude","CAP_FACE",FACE,{"disambiguationData":[OSD([subQ13,subQ12,subQ11,subQ10,subQ9,subQ8,subQ7,subQ6,subQ5,subQ4,subQ3,subQ2,subQ1,subQ0,sQuery(id+"F7.wireOp",EDGE,"E133")])],"isStart":true})]});}
            var sketch = newSketch(context, id + "F17", { "sketchPlane" : qUnion([Q0])});
            skArc(sketch, "E160", {"start": v(67.55, 13.22) * mm, "mid": v(75.44, 8.12) * mm, "end": v(83.32, 13.22) * mm});
            skLineSegment(sketch, "E161", {"start": v(75.44, 13.22) * mm, "end": v(75.44, 25.28) * mm, "construction": true});
            skLineSegment(sketch, "E162", {"start": v(67.55, 13.22) * mm, "end": v(83.32, 13.22) * mm});
            skPoint(sketch, "E163", {"position": v(75.44, 19.25) * mm});
            skSolve(sketch);
        }
        {
            var Q0;
            Q0=qSketchRegion(id+"F17",true);
            extrude(context, id + "F18", {"entities" : qUnion([Q0]), "operationType" : NewBodyOperationType.ADD, "oppositeDirection" : true, "depth" : 3.56 * mm});
        }
        {
            var Q0;
            Q0=makeQuery(id+"F12.boolean.opBoolean","COPY",EDGE,{"derivedFrom":makeQuery(id+"F12.opExtrude","CAP_EDGE",EDGE,{"disambiguationData":[OSD([sQuery(id+"F11.wireOp",EDGE,"E151")])],"isStart":false})});
            var Q1;
            Q1=makeQuery(id+"F12.boolean.opBoolean","COPY",EDGE,{"derivedFrom":makeQuery(id+"F12.opExtrude","CAP_EDGE",EDGE,{"disambiguationData":[OSD([sQuery(id+"F11.wireOp",EDGE,"E148.top")])],"isStart":false})});
            var Q2;
            Q2=makeQuery(id+"F12.boolean.opBoolean","COPY",EDGE,{"derivedFrom":makeQuery(id+"F12.opExtrude","CAP_EDGE",EDGE,{"disambiguationData":[OSD([sQuery(id+"F11.wireOp",EDGE,"E147.right")])],"isStart":false})});
            var Q3;
            Q3=makeQuery(id+"F16.boolean.opBoolean","COPY",EDGE,{"derivedFrom":makeQuery(id+"F16.opExtrude","CAP_EDGE",EDGE,{"disambiguationData":[OSD([sQuery(id+"F15.wireOp",EDGE,"E159.bottom")])],"isStart":false})});
            var Q4;
            Q4=makeQuery(id+"F18.opExtrude","CAP_EDGE",EDGE,{"disambiguationData":[OSD([sQuery(id+"F17.wireOp",EDGE,"E162")])],"isStart":false});
            var Q5;
            Q5=makeQuery(id+"F12.boolean.opBoolean","COPY",EDGE,{"derivedFrom":makeQuery(id+"F12.opExtrude","CAP_EDGE",EDGE,{"disambiguationData":[OSD([sQuery(id+"F11.wireOp",EDGE,"E149.bottom")])],"isStart":false})});
            var Q6;
            Q6=makeQuery(id+"F12.boolean.opBoolean","COPY",EDGE,{"derivedFrom":makeQuery(id+"F12.opExtrude","CAP_EDGE",EDGE,{"disambiguationData":[OSD([sQuery(id+"F11.wireOp",EDGE,"E150.top")])],"isStart":false})});
            var Q7;
            Q7=makeQuery(id+"F12.boolean.opBoolean","COPY",EDGE,{"derivedFrom":makeQuery(id+"F12.opExtrude","CAP_EDGE",EDGE,{"disambiguationData":[OSD([sQuery(id+"F11.wireOp",EDGE,"E155")])],"isStart":false})});
            var Q8;
            {var subQ1=sQuery(id+"F11.wireOp",EDGE,"E138");var subQ2=sQuery(id+"F0.wireOp",EDGE,"E10");Q8=makeQuery(id+"F12.boolean.opBoolean","COPY",EDGE,{"disambiguationData":[TD([makeQuery(id+"F1.opExtrude","SWEPT_FACE",FACE,{"disambiguationData":[OSD([subQ2])]})])],"derivedFrom":makeQuery(id+"F12.opExtrude","CAP_EDGE",EDGE,{"disambiguationData":[OSD([subQ1])],"isStart":false})});}
            var Q9;
            {var subQ0=sQuery(id+"F0.wireOp",EDGE,"E14");var subQ2=sQuery(id+"F11.wireOp",EDGE,"E138");Q9=makeQuery(id+"F12.boolean.opBoolean","COPY",EDGE,{"disambiguationData":[TD([makeQuery(id+"F1.opExtrude","SWEPT_FACE",FACE,{"disambiguationData":[OSD([subQ0])]})])],"derivedFrom":makeQuery(id+"F12.opExtrude","CAP_EDGE",EDGE,{"disambiguationData":[OSD([subQ2])],"isStart":false})});}
            var Q10;
            {var subQ3=sQuery(id+"F0.wireOp",EDGE,"E20");var subQ6=sQuery(id+"F11.wireOp",EDGE,"E136.bottom");Q10=makeQuery(id+"F12.boolean.opBoolean","COPY",EDGE,{"disambiguationData":[TD([makeQuery(id+"F1.opExtrude","SWEPT_FACE",FACE,{"disambiguationData":[OSD([subQ3])]})])],"derivedFrom":makeQuery(id+"F12.opExtrude","CAP_EDGE",EDGE,{"disambiguationData":[OSD([subQ6])],"isStart":false})});}
            var Q11;
            {var subQ3=sQuery(id+"F0.wireOp",EDGE,"E24");var subQ6=sQuery(id+"F11.wireOp",EDGE,"E136.bottom");Q11=makeQuery(id+"F12.boolean.opBoolean","COPY",EDGE,{"disambiguationData":[TD([makeQuery(id+"F1.opExtrude","SWEPT_FACE",FACE,{"disambiguationData":[OSD([subQ3])]})])],"derivedFrom":makeQuery(id+"F12.opExtrude","CAP_EDGE",EDGE,{"disambiguationData":[OSD([subQ6])],"isStart":false})});}
            var Q12;
            {var subQ0=sQuery(id+"F0.wireOp",EDGE,"E28");var subQ6=sQuery(id+"F11.wireOp",EDGE,"E136.bottom");Q12=makeQuery(id+"F12.boolean.opBoolean","COPY",EDGE,{"disambiguationData":[TD([makeQuery(id+"F1.opExtrude","SWEPT_FACE",FACE,{"disambiguationData":[OSD([subQ0])]})])],"derivedFrom":makeQuery(id+"F12.opExtrude","CAP_EDGE",EDGE,{"disambiguationData":[OSD([subQ6])],"isStart":false})});}
            var Q13;
            Q13=makeQuery(id+"F12.boolean.opBoolean","COPY",EDGE,{"derivedFrom":makeQuery(id+"F12.opExtrude","CAP_EDGE",EDGE,{"disambiguationData":[OSD([sQuery(id+"F11.wireOp",EDGE,"E142.bottom")])],"isStart":false})});
            var Q14;
            {var subQ2=sQuery(id+"F0.wireOp",EDGE,"E66");var subQ3=sQuery(id+"F11.wireOp",EDGE,"E137.bottom");Q14=makeQuery(id+"F12.boolean.opBoolean","COPY",EDGE,{"disambiguationData":[TD([makeQuery(id+"F1.opExtrude","SWEPT_FACE",FACE,{"disambiguationData":[OSD([subQ2])]})])],"derivedFrom":makeQuery(id+"F12.opExtrude","CAP_EDGE",EDGE,{"disambiguationData":[OSD([subQ3])],"isStart":false})});}
            var Q15;
            {var subQ2=sQuery(id+"F11.wireOp",EDGE,"E137.bottom");var subQ5=sQuery(id+"F0.wireOp",EDGE,"E70");Q15=makeQuery(id+"F12.boolean.opBoolean","COPY",EDGE,{"disambiguationData":[TD([makeQuery(id+"F1.opExtrude","SWEPT_FACE",FACE,{"disambiguationData":[OSD([subQ5])]})])],"derivedFrom":makeQuery(id+"F12.opExtrude","CAP_EDGE",EDGE,{"disambiguationData":[OSD([subQ2])],"isStart":false})});}
            var Q16;
            {var subQ3=sQuery(id+"F0.wireOp",EDGE,"E34");var subQ4=sQuery(id+"F11.wireOp",EDGE,"E146");Q16=makeQuery(id+"F12.boolean.opBoolean","COPY",EDGE,{"disambiguationData":[TD([makeQuery(id+"F1.opExtrude","SWEPT_FACE",FACE,{"disambiguationData":[OSD([subQ3])]})])],"derivedFrom":makeQuery(id+"F12.opExtrude","CAP_EDGE",EDGE,{"disambiguationData":[OSD([subQ4])],"isStart":false})});}
            var Q17;
            {var subQ4=sQuery(id+"F11.wireOp",EDGE,"E146");var subQ5=sQuery(id+"F0.wireOp",EDGE,"E38");Q17=makeQuery(id+"F12.boolean.opBoolean","COPY",EDGE,{"disambiguationData":[TD([makeQuery(id+"F1.opExtrude","SWEPT_FACE",FACE,{"disambiguationData":[OSD([subQ5])]})])],"derivedFrom":makeQuery(id+"F12.opExtrude","CAP_EDGE",EDGE,{"disambiguationData":[OSD([subQ4])],"isStart":false})});}
            var Q18;
            {var subQ2=sQuery(id+"F11.wireOp",EDGE,"E144");var subQ5=sQuery(id+"F0.wireOp",EDGE,"E60");Q18=makeQuery(id+"F12.boolean.opBoolean","COPY",EDGE,{"disambiguationData":[TD([makeQuery(id+"F1.opExtrude","SWEPT_FACE",FACE,{"disambiguationData":[OSD([subQ5])]})])],"derivedFrom":makeQuery(id+"F12.opExtrude","CAP_EDGE",EDGE,{"disambiguationData":[OSD([subQ2])],"isStart":false})});}
            var Q19;
            {var subQ1=sQuery(id+"F0.wireOp",EDGE,"E56");var subQ4=sQuery(id+"F11.wireOp",EDGE,"E144");Q19=makeQuery(id+"F12.boolean.opBoolean","COPY",EDGE,{"disambiguationData":[TD([makeQuery(id+"F1.opExtrude","SWEPT_FACE",FACE,{"disambiguationData":[OSD([subQ1])]})])],"derivedFrom":makeQuery(id+"F12.opExtrude","CAP_EDGE",EDGE,{"disambiguationData":[OSD([subQ4])],"isStart":false})});}
            fillet(context, id + "F19", {"entities" : qUnion([Q0, Q1, Q2, Q3, Q4, Q5, Q6, Q7, Q8, Q9, Q10, Q11, Q12, Q13, Q14, Q15, Q16, Q17, Q18, Q19]), "radius" : 0.25 * mm, "tangentPropagation" : true, "allowEdgeOverflow" : false});
        }
        {
            var Q0;
            {var subQ0=sQuery(id+"F0.wireOp",EDGE,"E30");Q0=makeQuery(id+"F4.boolean.opBoolean","MERGE",FACE,{"derivedFrom":[makeQuery(id+"F1.opExtrude","SWEPT_FACE",FACE,{"disambiguationData":[OSD([subQ0])]}),makeQuery(id+"F4.opExtrude","SWEPT_FACE",FACE,{"disambiguationData":[OSD([subQ0])]})]});}
            cPlane(context, id + "F20", {"entities" : qUnion([Q0]), "cplaneType" : CPlaneType.OFFSET, "offset" : 1.59 * mm, "oppositeDirection" : true, "width" : 152.4 * mm, "height" : 152.4 * mm});
        }
        {
            var Q0;
            Q0=qCreatedBy(id+"F20.planeOp",FACE);
            var sketch = newSketch(context, id + "F21", { "sketchPlane" : qUnion([Q0])});
            skLineSegment(sketch, "E164.bottom", {"start": v(-46.24, 12.7) * mm, "end": v(-50.68, 12.7) * mm});
            skLineSegment(sketch, "E164.top", {"start": v(-46.24, 14.22) * mm, "end": v(-50.68, 14.22) * mm});
            skLineSegment(sketch, "E164.left", {"start": v(-46.24, 12.7) * mm, "end": v(-46.24, 14.22) * mm});
            skLineSegment(sketch, "E164.right", {"start": v(-50.68, 12.7) * mm, "end": v(-50.68, 14.22) * mm});
            skLineSegment(sketch, "E165", {"start": v(-50.68, 14.22) * mm, "end": v(-50.68, 17.14) * mm});
            skLineSegment(sketch, "E166", {"start": v(-50.68, 17.14) * mm, "end": v(-46.24, 14.22) * mm});
            skSolve(sketch);
        }
        {
            var Q0;
            Q0=qSketchRegion(id+"F21",true);
            extrude(context, id + "F22", {"entities" : qUnion([Q0]), "oppositeDirection" : true, "depth" : 4.76 * mm});
        }
        {
            var Q0;
            {var subQ0=sQuery(id+"F0.wireOp",EDGE,"E26");Q0=makeQuery(id+"F4.boolean.opBoolean","MERGE",FACE,{"derivedFrom":[makeQuery(id+"F1.opExtrude","SWEPT_FACE",FACE,{"disambiguationData":[OSD([subQ0])]}),makeQuery(id+"F4.opExtrude","SWEPT_FACE",FACE,{"disambiguationData":[OSD([subQ0])]})]});}
            cPlane(context, id + "F23", {"entities" : qUnion([Q0]), "cplaneType" : CPlaneType.OFFSET, "offset" : 0 * mm, "oppositeDirection" : true, "width" : 152.4 * mm, "height" : 152.4 * mm});
        }
        {
            var Q0;
            Q0=qCreatedBy(id+"F23.planeOp",FACE);
            var sketch = newSketch(context, id + "F24", { "sketchPlane" : qUnion([Q0])});
            skLineSegment(sketch, "E167.0.0", {"start": v(-50.68, 12.7) * mm, "end": v(-46.24, 12.7) * mm});
            skLineSegment(sketch, "E167.0.1", {"start": v(-46.24, 12.7) * mm, "end": v(-46.24, 14.22) * mm});
            skLineSegment(sketch, "E167.0.2", {"start": v(-46.24, 14.22) * mm, "end": v(-50.68, 17.14) * mm});
            skLineSegment(sketch, "E167.0.3", {"start": v(-50.68, 17.14) * mm, "end": v(-50.68, 12.7) * mm});
            skSolve(sketch);
        }
        {
            var Q0;
            Q0=qSketchRegion(id+"F24",true);
            var Q1;
            {var subQ0=sQuery(id+"F0.wireOp",EDGE,"E24");Q1=makeQuery(id+"F4.boolean.opBoolean","MERGE",FACE,{"derivedFrom":[makeQuery(id+"F1.opExtrude","SWEPT_FACE",FACE,{"disambiguationData":[OSD([subQ0])]}),makeQuery(id+"F4.opExtrude","SWEPT_FACE",FACE,{"disambiguationData":[OSD([subQ0])]})]});}
            extrude(context, id + "F25", {"entities" : qUnion([Q0]), "operationType" : NewBodyOperationType.ADD, "endBound" : BoundingType.UP_TO_SURFACE, "oppositeDirection" : true, "endBoundEntityFace" : qUnion([Q1]), "depth" : 25.4 * mm});
        }
    });
